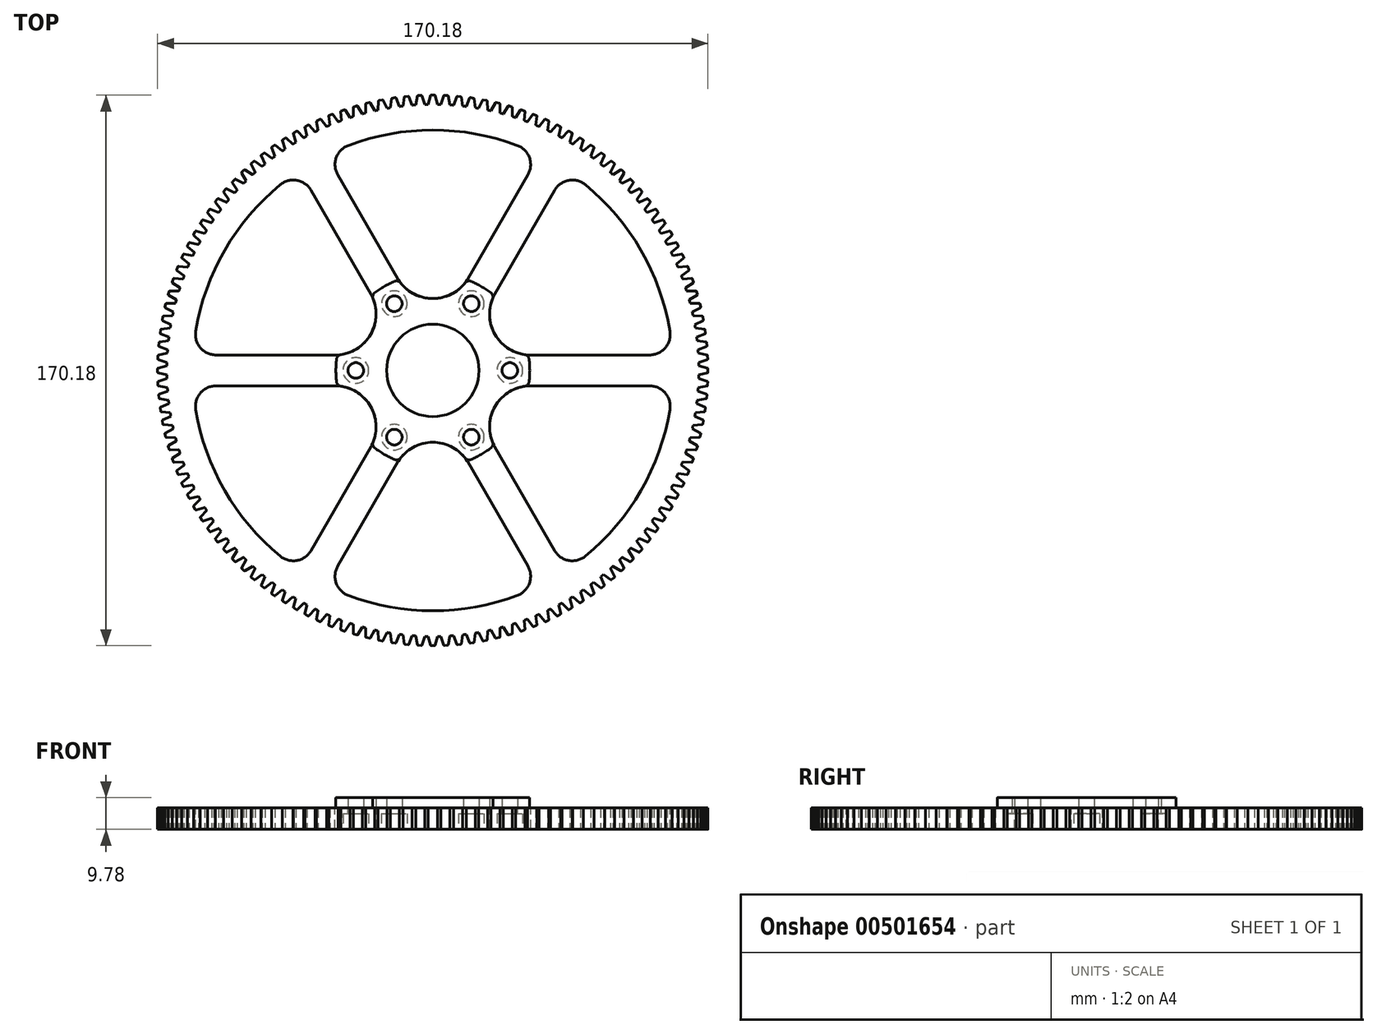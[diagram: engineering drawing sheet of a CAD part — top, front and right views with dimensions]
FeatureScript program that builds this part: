
annotation { "Feature Type Name" : "Feature", "Feature Type Description" : "" }
export const myFeature = defineFeature(function(context is Context, id is Id, definition is map)
    precondition{}
    {
        {
            var Q0;
            Q0=qCreatedBy(makeId("Top.planeOp"),FACE);
            var sketch = newSketch(context, id + "F0", { "sketchPlane" : qUnion([Q0])});
            skArc(sketch, "E0", {"start": v(-1.4, 82.23) * mm, "mid": v(-82.23, -1.4) * mm, "end": v(1.4, -82.23) * mm});
            skArc(sketch, "E1", {"start": v(1.4, -82.23) * mm, "mid": v(82.24, 0) * mm, "end": v(1.4, 82.23) * mm});
            skLineSegment(sketch, "E2", {"start": v(1.4, 82.23) * mm, "end": v(0.7, 84.97) * mm});
            skArc(sketch, "E3", {"start": v(0.7, 84.97) * mm, "mid": v(0.64, 85.06) * mm, "end": v(0.55, 85.1) * mm});
            skLineSegment(sketch, "E4", {"start": v(-1.4, 82.23) * mm, "end": v(-0.7, 84.97) * mm});
            skArc(sketch, "E5", {"start": v(-0.55, 85.1) * mm, "mid": v(-0.64, 85.06) * mm, "end": v(-0.7, 84.97) * mm});
            skLineSegment(sketch, "E6", {"start": v(-0.55, 85.1) * mm, "end": v(0.55, 85.1) * mm});
            skArc(sketch, "E7", {"start": v(1.4, 82.23) * mm, "mid": v(0, 82.24) * mm, "end": v(-1.4, 82.23) * mm});
            skSolve(sketch);
        }
        {
            var Q0;
            Q0=makeQuery(id+"F0.imprint","IMPRINT",FACE,{"disambiguationData":[TD([[makeQuery(id+"F0.imprint","IMPRINT",EDGE,{"derivedFrom":sQuery(id+"F0.wireOp",EDGE,"E0")}),1.0]])]});
            extrude(context, id + "F1", {"entities" : qUnion([Q0]), "endBound" : BoundingType.SYMMETRIC, "depth" : 6.6 * mm});
        }
        {
            var Q0;
            Q0=makeQuery(id+"F0.imprint","IMPRINT",FACE,{"disambiguationData":[TD([[makeQuery(id+"F0.imprint","IMPRINT",EDGE,{"derivedFrom":sQuery(id+"F0.wireOp",EDGE,"E2")}),1.0]])]});
            var Q1;
            Q1=makeQuery(id+"F1.opExtrude","CAP_FACE",FACE,{"disambiguationData":[OSD([sQuery(id+"F0.wireOp",EDGE,"E0"),sQuery(id+"F0.wireOp",EDGE,"E1"),sQuery(id+"F0.wireOp",EDGE,"E7")])],"isStart":false});
            var Q2;
            Q2=makeQuery(id+"F1.opExtrude","CAP_FACE",FACE,{"disambiguationData":[OSD([sQuery(id+"F0.wireOp",EDGE,"E0"),sQuery(id+"F0.wireOp",EDGE,"E1"),sQuery(id+"F0.wireOp",EDGE,"E7")])],"isStart":true});
            extrude(context, id + "F2", {"entities" : qUnion([Q0]), "endBound" : BoundingType.UP_TO_SURFACE, "endBoundEntityFace" : qUnion([Q1]), "depth" : 25.4 * mm, "hasSecondDirection" : true, "secondDirectionBound" : SecondDirectionBoundingType.UP_TO_SURFACE, "secondDirectionOppositeDirection" : true, "secondDirectionBoundEntityFace" : qUnion([Q2]), "secondDirectionDepth" : 25.4 * mm});
        }
        {
            var Q0;
            Q0=makeQuery(id+"F2.opExtrude","SWEPT_BODY",BODY,{"disambiguationData":[OSD([sQuery(id+"F0.wireOp",EDGE,"E2"),sQuery(id+"F0.wireOp",EDGE,"E3"),sQuery(id+"F0.wireOp",EDGE,"E4"),sQuery(id+"F0.wireOp",EDGE,"E5"),sQuery(id+"F0.wireOp",EDGE,"E6"),sQuery(id+"F0.wireOp",EDGE,"E7")])]});
            var Q1;
            Q1=makeQuery(id+"F1.opExtrude","CAP_EDGE",EDGE,{"disambiguationData":[OSD([sQuery(id+"F0.wireOp",EDGE,"E0"),sQuery(id+"F0.wireOp",EDGE,"E1"),sQuery(id+"F0.wireOp",EDGE,"E7")])],"isStart":false});
            circularPattern(context, id + "F3", {"operationType" : NewBodyOperationType.ADD, "entities" : qUnion([Q0]), "axis" : qUnion([Q1]), "angle" : 360 * degree, "instanceCount" : 132, "oppositeDirection" : true, "equalSpace" : true});
        }
        {
            var Q0;
            {var subQ0=sQuery(id+"F0.wireOp",EDGE,"E7");var subQ1=makeQuery(id+"F2.opExtrude","CAP_FACE",FACE,{"disambiguationData":[OSD([sQuery(id+"F0.wireOp",EDGE,"E2"),sQuery(id+"F0.wireOp",EDGE,"E3"),sQuery(id+"F0.wireOp",EDGE,"E4"),sQuery(id+"F0.wireOp",EDGE,"E5"),sQuery(id+"F0.wireOp",EDGE,"E6"),subQ0])],"isStart":false});Q0=makeQuery(id+"F3.boolean.opBoolean","MERGE",FACE,{"derivedFrom":[makeQuery(id+"F1.opExtrude","CAP_FACE",FACE,{"disambiguationData":[OSD([sQuery(id+"F0.wireOp",EDGE,"E0"),sQuery(id+"F0.wireOp",EDGE,"E1"),subQ0])],"isStart":false}),subQ1,makeQuery(id+"F3.opPattern","COPY",FACE,{"derivedFrom":subQ1,"instanceName":"1"}),makeQuery(id+"F3.opPattern","COPY",FACE,{"derivedFrom":subQ1,"instanceName":"2"}),makeQuery(id+"F3.opPattern","COPY",FACE,{"derivedFrom":subQ1,"instanceName":"3"}),makeQuery(id+"F3.opPattern","COPY",FACE,{"derivedFrom":subQ1,"instanceName":"4"}),makeQuery(id+"F3.opPattern","COPY",FACE,{"derivedFrom":subQ1,"instanceName":"5"}),makeQuery(id+"F3.opPattern","COPY",FACE,{"derivedFrom":subQ1,"instanceName":"6"}),makeQuery(id+"F3.opPattern","COPY",FACE,{"derivedFrom":subQ1,"instanceName":"7"}),makeQuery(id+"F3.opPattern","COPY",FACE,{"derivedFrom":subQ1,"instanceName":"8"}),makeQuery(id+"F3.opPattern","COPY",FACE,{"derivedFrom":subQ1,"instanceName":"9"}),makeQuery(id+"F3.opPattern","COPY",FACE,{"derivedFrom":subQ1,"instanceName":"10"}),makeQuery(id+"F3.opPattern","COPY",FACE,{"derivedFrom":subQ1,"instanceName":"11"}),makeQuery(id+"F3.opPattern","COPY",FACE,{"derivedFrom":subQ1,"instanceName":"12"}),makeQuery(id+"F3.opPattern","COPY",FACE,{"derivedFrom":subQ1,"instanceName":"13"}),makeQuery(id+"F3.opPattern","COPY",FACE,{"derivedFrom":subQ1,"instanceName":"14"}),makeQuery(id+"F3.opPattern","COPY",FACE,{"derivedFrom":subQ1,"instanceName":"15"}),makeQuery(id+"F3.opPattern","COPY",FACE,{"derivedFrom":subQ1,"instanceName":"16"}),makeQuery(id+"F3.opPattern","COPY",FACE,{"derivedFrom":subQ1,"instanceName":"17"}),makeQuery(id+"F3.opPattern","COPY",FACE,{"derivedFrom":subQ1,"instanceName":"18"}),makeQuery(id+"F3.opPattern","COPY",FACE,{"derivedFrom":subQ1,"instanceName":"19"}),makeQuery(id+"F3.opPattern","COPY",FACE,{"derivedFrom":subQ1,"instanceName":"20"}),makeQuery(id+"F3.opPattern","COPY",FACE,{"derivedFrom":subQ1,"instanceName":"21"}),makeQuery(id+"F3.opPattern","COPY",FACE,{"derivedFrom":subQ1,"instanceName":"22"}),makeQuery(id+"F3.opPattern","COPY",FACE,{"derivedFrom":subQ1,"instanceName":"23"}),makeQuery(id+"F3.opPattern","COPY",FACE,{"derivedFrom":subQ1,"instanceName":"24"}),makeQuery(id+"F3.opPattern","COPY",FACE,{"derivedFrom":subQ1,"instanceName":"25"}),makeQuery(id+"F3.opPattern","COPY",FACE,{"derivedFrom":subQ1,"instanceName":"26"}),makeQuery(id+"F3.opPattern","COPY",FACE,{"derivedFrom":subQ1,"instanceName":"27"}),makeQuery(id+"F3.opPattern","COPY",FACE,{"derivedFrom":subQ1,"instanceName":"28"}),makeQuery(id+"F3.opPattern","COPY",FACE,{"derivedFrom":subQ1,"instanceName":"29"}),makeQuery(id+"F3.opPattern","COPY",FACE,{"derivedFrom":subQ1,"instanceName":"30"}),makeQuery(id+"F3.opPattern","COPY",FACE,{"derivedFrom":subQ1,"instanceName":"31"}),makeQuery(id+"F3.opPattern","COPY",FACE,{"derivedFrom":subQ1,"instanceName":"32"}),makeQuery(id+"F3.opPattern","COPY",FACE,{"derivedFrom":subQ1,"instanceName":"33"}),makeQuery(id+"F3.opPattern","COPY",FACE,{"derivedFrom":subQ1,"instanceName":"34"}),makeQuery(id+"F3.opPattern","COPY",FACE,{"derivedFrom":subQ1,"instanceName":"35"}),makeQuery(id+"F3.opPattern","COPY",FACE,{"derivedFrom":subQ1,"instanceName":"36"}),makeQuery(id+"F3.opPattern","COPY",FACE,{"derivedFrom":subQ1,"instanceName":"37"}),makeQuery(id+"F3.opPattern","COPY",FACE,{"derivedFrom":subQ1,"instanceName":"38"}),makeQuery(id+"F3.opPattern","COPY",FACE,{"derivedFrom":subQ1,"instanceName":"39"}),makeQuery(id+"F3.opPattern","COPY",FACE,{"derivedFrom":subQ1,"instanceName":"40"}),makeQuery(id+"F3.opPattern","COPY",FACE,{"derivedFrom":subQ1,"instanceName":"41"}),makeQuery(id+"F3.opPattern","COPY",FACE,{"derivedFrom":subQ1,"instanceName":"42"}),makeQuery(id+"F3.opPattern","COPY",FACE,{"derivedFrom":subQ1,"instanceName":"43"}),makeQuery(id+"F3.opPattern","COPY",FACE,{"derivedFrom":subQ1,"instanceName":"44"}),makeQuery(id+"F3.opPattern","COPY",FACE,{"derivedFrom":subQ1,"instanceName":"45"}),makeQuery(id+"F3.opPattern","COPY",FACE,{"derivedFrom":subQ1,"instanceName":"46"}),makeQuery(id+"F3.opPattern","COPY",FACE,{"derivedFrom":subQ1,"instanceName":"47"}),makeQuery(id+"F3.opPattern","COPY",FACE,{"derivedFrom":subQ1,"instanceName":"48"}),makeQuery(id+"F3.opPattern","COPY",FACE,{"derivedFrom":subQ1,"instanceName":"49"}),makeQuery(id+"F3.opPattern","COPY",FACE,{"derivedFrom":subQ1,"instanceName":"50"}),makeQuery(id+"F3.opPattern","COPY",FACE,{"derivedFrom":subQ1,"instanceName":"51"}),makeQuery(id+"F3.opPattern","COPY",FACE,{"derivedFrom":subQ1,"instanceName":"52"}),makeQuery(id+"F3.opPattern","COPY",FACE,{"derivedFrom":subQ1,"instanceName":"53"}),makeQuery(id+"F3.opPattern","COPY",FACE,{"derivedFrom":subQ1,"instanceName":"54"}),makeQuery(id+"F3.opPattern","COPY",FACE,{"derivedFrom":subQ1,"instanceName":"55"}),makeQuery(id+"F3.opPattern","COPY",FACE,{"derivedFrom":subQ1,"instanceName":"56"}),makeQuery(id+"F3.opPattern","COPY",FACE,{"derivedFrom":subQ1,"instanceName":"57"}),makeQuery(id+"F3.opPattern","COPY",FACE,{"derivedFrom":subQ1,"instanceName":"58"}),makeQuery(id+"F3.opPattern","COPY",FACE,{"derivedFrom":subQ1,"instanceName":"59"}),makeQuery(id+"F3.opPattern","COPY",FACE,{"derivedFrom":subQ1,"instanceName":"60"}),makeQuery(id+"F3.opPattern","COPY",FACE,{"derivedFrom":subQ1,"instanceName":"61"}),makeQuery(id+"F3.opPattern","COPY",FACE,{"derivedFrom":subQ1,"instanceName":"62"}),makeQuery(id+"F3.opPattern","COPY",FACE,{"derivedFrom":subQ1,"instanceName":"63"}),makeQuery(id+"F3.opPattern","COPY",FACE,{"derivedFrom":subQ1,"instanceName":"64"}),makeQuery(id+"F3.opPattern","COPY",FACE,{"derivedFrom":subQ1,"instanceName":"65"}),makeQuery(id+"F3.opPattern","COPY",FACE,{"derivedFrom":subQ1,"instanceName":"66"}),makeQuery(id+"F3.opPattern","COPY",FACE,{"derivedFrom":subQ1,"instanceName":"67"}),makeQuery(id+"F3.opPattern","COPY",FACE,{"derivedFrom":subQ1,"instanceName":"68"}),makeQuery(id+"F3.opPattern","COPY",FACE,{"derivedFrom":subQ1,"instanceName":"69"}),makeQuery(id+"F3.opPattern","COPY",FACE,{"derivedFrom":subQ1,"instanceName":"70"}),makeQuery(id+"F3.opPattern","COPY",FACE,{"derivedFrom":subQ1,"instanceName":"71"}),makeQuery(id+"F3.opPattern","COPY",FACE,{"derivedFrom":subQ1,"instanceName":"72"}),makeQuery(id+"F3.opPattern","COPY",FACE,{"derivedFrom":subQ1,"instanceName":"73"}),makeQuery(id+"F3.opPattern","COPY",FACE,{"derivedFrom":subQ1,"instanceName":"74"}),makeQuery(id+"F3.opPattern","COPY",FACE,{"derivedFrom":subQ1,"instanceName":"75"}),makeQuery(id+"F3.opPattern","COPY",FACE,{"derivedFrom":subQ1,"instanceName":"76"}),makeQuery(id+"F3.opPattern","COPY",FACE,{"derivedFrom":subQ1,"instanceName":"77"}),makeQuery(id+"F3.opPattern","COPY",FACE,{"derivedFrom":subQ1,"instanceName":"78"}),makeQuery(id+"F3.opPattern","COPY",FACE,{"derivedFrom":subQ1,"instanceName":"79"}),makeQuery(id+"F3.opPattern","COPY",FACE,{"derivedFrom":subQ1,"instanceName":"80"}),makeQuery(id+"F3.opPattern","COPY",FACE,{"derivedFrom":subQ1,"instanceName":"81"}),makeQuery(id+"F3.opPattern","COPY",FACE,{"derivedFrom":subQ1,"instanceName":"82"}),makeQuery(id+"F3.opPattern","COPY",FACE,{"derivedFrom":subQ1,"instanceName":"83"}),makeQuery(id+"F3.opPattern","COPY",FACE,{"derivedFrom":subQ1,"instanceName":"84"}),makeQuery(id+"F3.opPattern","COPY",FACE,{"derivedFrom":subQ1,"instanceName":"85"}),makeQuery(id+"F3.opPattern","COPY",FACE,{"derivedFrom":subQ1,"instanceName":"86"}),makeQuery(id+"F3.opPattern","COPY",FACE,{"derivedFrom":subQ1,"instanceName":"87"}),makeQuery(id+"F3.opPattern","COPY",FACE,{"derivedFrom":subQ1,"instanceName":"88"}),makeQuery(id+"F3.opPattern","COPY",FACE,{"derivedFrom":subQ1,"instanceName":"89"}),makeQuery(id+"F3.opPattern","COPY",FACE,{"derivedFrom":subQ1,"instanceName":"90"}),makeQuery(id+"F3.opPattern","COPY",FACE,{"derivedFrom":subQ1,"instanceName":"91"}),makeQuery(id+"F3.opPattern","COPY",FACE,{"derivedFrom":subQ1,"instanceName":"92"}),makeQuery(id+"F3.opPattern","COPY",FACE,{"derivedFrom":subQ1,"instanceName":"93"}),makeQuery(id+"F3.opPattern","COPY",FACE,{"derivedFrom":subQ1,"instanceName":"94"}),makeQuery(id+"F3.opPattern","COPY",FACE,{"derivedFrom":subQ1,"instanceName":"95"}),makeQuery(id+"F3.opPattern","COPY",FACE,{"derivedFrom":subQ1,"instanceName":"96"}),makeQuery(id+"F3.opPattern","COPY",FACE,{"derivedFrom":subQ1,"instanceName":"97"}),makeQuery(id+"F3.opPattern","COPY",FACE,{"derivedFrom":subQ1,"instanceName":"98"}),makeQuery(id+"F3.opPattern","COPY",FACE,{"derivedFrom":subQ1,"instanceName":"99"}),makeQuery(id+"F3.opPattern","COPY",FACE,{"derivedFrom":subQ1,"instanceName":"100"}),makeQuery(id+"F3.opPattern","COPY",FACE,{"derivedFrom":subQ1,"instanceName":"101"}),makeQuery(id+"F3.opPattern","COPY",FACE,{"derivedFrom":subQ1,"instanceName":"102"}),makeQuery(id+"F3.opPattern","COPY",FACE,{"derivedFrom":subQ1,"instanceName":"103"}),makeQuery(id+"F3.opPattern","COPY",FACE,{"derivedFrom":subQ1,"instanceName":"104"}),makeQuery(id+"F3.opPattern","COPY",FACE,{"derivedFrom":subQ1,"instanceName":"105"}),makeQuery(id+"F3.opPattern","COPY",FACE,{"derivedFrom":subQ1,"instanceName":"106"}),makeQuery(id+"F3.opPattern","COPY",FACE,{"derivedFrom":subQ1,"instanceName":"107"}),makeQuery(id+"F3.opPattern","COPY",FACE,{"derivedFrom":subQ1,"instanceName":"108"}),makeQuery(id+"F3.opPattern","COPY",FACE,{"derivedFrom":subQ1,"instanceName":"109"}),makeQuery(id+"F3.opPattern","COPY",FACE,{"derivedFrom":subQ1,"instanceName":"110"}),makeQuery(id+"F3.opPattern","COPY",FACE,{"derivedFrom":subQ1,"instanceName":"111"}),makeQuery(id+"F3.opPattern","COPY",FACE,{"derivedFrom":subQ1,"instanceName":"112"}),makeQuery(id+"F3.opPattern","COPY",FACE,{"derivedFrom":subQ1,"instanceName":"113"}),makeQuery(id+"F3.opPattern","COPY",FACE,{"derivedFrom":subQ1,"instanceName":"114"}),makeQuery(id+"F3.opPattern","COPY",FACE,{"derivedFrom":subQ1,"instanceName":"115"}),makeQuery(id+"F3.opPattern","COPY",FACE,{"derivedFrom":subQ1,"instanceName":"116"}),makeQuery(id+"F3.opPattern","COPY",FACE,{"derivedFrom":subQ1,"instanceName":"117"}),makeQuery(id+"F3.opPattern","COPY",FACE,{"derivedFrom":subQ1,"instanceName":"118"}),makeQuery(id+"F3.opPattern","COPY",FACE,{"derivedFrom":subQ1,"instanceName":"119"}),makeQuery(id+"F3.opPattern","COPY",FACE,{"derivedFrom":subQ1,"instanceName":"120"}),makeQuery(id+"F3.opPattern","COPY",FACE,{"derivedFrom":subQ1,"instanceName":"121"}),makeQuery(id+"F3.opPattern","COPY",FACE,{"derivedFrom":subQ1,"instanceName":"122"}),makeQuery(id+"F3.opPattern","COPY",FACE,{"derivedFrom":subQ1,"instanceName":"123"}),makeQuery(id+"F3.opPattern","COPY",FACE,{"derivedFrom":subQ1,"instanceName":"124"}),makeQuery(id+"F3.opPattern","COPY",FACE,{"derivedFrom":subQ1,"instanceName":"125"}),makeQuery(id+"F3.opPattern","COPY",FACE,{"derivedFrom":subQ1,"instanceName":"126"}),makeQuery(id+"F3.opPattern","COPY",FACE,{"derivedFrom":subQ1,"instanceName":"127"}),makeQuery(id+"F3.opPattern","COPY",FACE,{"derivedFrom":subQ1,"instanceName":"128"}),makeQuery(id+"F3.opPattern","COPY",FACE,{"derivedFrom":subQ1,"instanceName":"129"}),makeQuery(id+"F3.opPattern","COPY",FACE,{"derivedFrom":subQ1,"instanceName":"130"}),makeQuery(id+"F3.opPattern","COPY",FACE,{"derivedFrom":subQ1,"instanceName":"131"})]});}
            var sketch = newSketch(context, id + "F4", { "sketchPlane" : qUnion([Q0])});
            skCircle(sketch, "E8", {"center": v(0, 0) * mm, "radius": 14.29 * mm});
            skCircle(sketch, "E9.cCircle", {"center": v(0, 0) * mm, "radius": 23.81 * mm, "construction": true});
            skLineSegment(sketch, "E9.0", {"start": v(23.81, 0) * mm, "end": v(11.9, -20.62) * mm, "construction": true});
            skLineSegment(sketch, "E9.1", {"start": v(11.9, -20.62) * mm, "end": v(-11.9, -20.62) * mm, "construction": true});
            skLineSegment(sketch, "E9.2", {"start": v(-11.9, -20.62) * mm, "end": v(-23.81, 0) * mm, "construction": true});
            skLineSegment(sketch, "E9.3", {"start": v(-23.81, 0) * mm, "end": v(-11.9, 20.62) * mm, "construction": true});
            skLineSegment(sketch, "E9.4", {"start": v(-11.9, 20.62) * mm, "end": v(11.9, 20.62) * mm, "construction": true});
            skLineSegment(sketch, "E9.5", {"start": v(11.9, 20.62) * mm, "end": v(23.81, 0) * mm, "construction": true});
            skCircle(sketch, "E10", {"center": v(-11.9, 20.62) * mm, "radius": 2.41 * mm});
            skCircle(sketch, "E11", {"center": v(-23.81, 0) * mm, "radius": 2.41 * mm});
            skCircle(sketch, "E12", {"center": v(-11.9, -20.62) * mm, "radius": 2.41 * mm});
            skCircle(sketch, "E13", {"center": v(11.9, -20.62) * mm, "radius": 2.41 * mm});
            skCircle(sketch, "E14", {"center": v(23.81, 0) * mm, "radius": 2.41 * mm});
            skCircle(sketch, "E15", {"center": v(11.9, 20.62) * mm, "radius": 2.41 * mm});
            skSolve(sketch);
        }
        {
            var Q0;
            Q0=qSketchRegion(id+"F4",true);
            extrude(context, id + "F5", {"entities" : qUnion([Q0]), "operationType" : NewBodyOperationType.REMOVE, "endBound" : BoundingType.THROUGH_ALL, "oppositeDirection" : true, "depth" : 25.4 * mm});
        }
        {
            var Q0;
            {var subQ0=sQuery(id+"F0.wireOp",EDGE,"E7");var subQ1=makeQuery(id+"F2.opExtrude","CAP_FACE",FACE,{"disambiguationData":[OSD([sQuery(id+"F0.wireOp",EDGE,"E2"),sQuery(id+"F0.wireOp",EDGE,"E3"),sQuery(id+"F0.wireOp",EDGE,"E4"),sQuery(id+"F0.wireOp",EDGE,"E5"),sQuery(id+"F0.wireOp",EDGE,"E6"),subQ0])],"isStart":false});Q0=makeQuery(id+"F3.boolean.opBoolean","MERGE",FACE,{"derivedFrom":[makeQuery(id+"F1.opExtrude","CAP_FACE",FACE,{"disambiguationData":[OSD([sQuery(id+"F0.wireOp",EDGE,"E0"),sQuery(id+"F0.wireOp",EDGE,"E1"),subQ0])],"isStart":false}),subQ1,makeQuery(id+"F3.opPattern","COPY",FACE,{"derivedFrom":subQ1,"instanceName":"1"}),makeQuery(id+"F3.opPattern","COPY",FACE,{"derivedFrom":subQ1,"instanceName":"2"}),makeQuery(id+"F3.opPattern","COPY",FACE,{"derivedFrom":subQ1,"instanceName":"3"}),makeQuery(id+"F3.opPattern","COPY",FACE,{"derivedFrom":subQ1,"instanceName":"4"}),makeQuery(id+"F3.opPattern","COPY",FACE,{"derivedFrom":subQ1,"instanceName":"5"}),makeQuery(id+"F3.opPattern","COPY",FACE,{"derivedFrom":subQ1,"instanceName":"6"}),makeQuery(id+"F3.opPattern","COPY",FACE,{"derivedFrom":subQ1,"instanceName":"7"}),makeQuery(id+"F3.opPattern","COPY",FACE,{"derivedFrom":subQ1,"instanceName":"8"}),makeQuery(id+"F3.opPattern","COPY",FACE,{"derivedFrom":subQ1,"instanceName":"9"}),makeQuery(id+"F3.opPattern","COPY",FACE,{"derivedFrom":subQ1,"instanceName":"10"}),makeQuery(id+"F3.opPattern","COPY",FACE,{"derivedFrom":subQ1,"instanceName":"11"}),makeQuery(id+"F3.opPattern","COPY",FACE,{"derivedFrom":subQ1,"instanceName":"12"}),makeQuery(id+"F3.opPattern","COPY",FACE,{"derivedFrom":subQ1,"instanceName":"13"}),makeQuery(id+"F3.opPattern","COPY",FACE,{"derivedFrom":subQ1,"instanceName":"14"}),makeQuery(id+"F3.opPattern","COPY",FACE,{"derivedFrom":subQ1,"instanceName":"15"}),makeQuery(id+"F3.opPattern","COPY",FACE,{"derivedFrom":subQ1,"instanceName":"16"}),makeQuery(id+"F3.opPattern","COPY",FACE,{"derivedFrom":subQ1,"instanceName":"17"}),makeQuery(id+"F3.opPattern","COPY",FACE,{"derivedFrom":subQ1,"instanceName":"18"}),makeQuery(id+"F3.opPattern","COPY",FACE,{"derivedFrom":subQ1,"instanceName":"19"}),makeQuery(id+"F3.opPattern","COPY",FACE,{"derivedFrom":subQ1,"instanceName":"20"}),makeQuery(id+"F3.opPattern","COPY",FACE,{"derivedFrom":subQ1,"instanceName":"21"}),makeQuery(id+"F3.opPattern","COPY",FACE,{"derivedFrom":subQ1,"instanceName":"22"}),makeQuery(id+"F3.opPattern","COPY",FACE,{"derivedFrom":subQ1,"instanceName":"23"}),makeQuery(id+"F3.opPattern","COPY",FACE,{"derivedFrom":subQ1,"instanceName":"24"}),makeQuery(id+"F3.opPattern","COPY",FACE,{"derivedFrom":subQ1,"instanceName":"25"}),makeQuery(id+"F3.opPattern","COPY",FACE,{"derivedFrom":subQ1,"instanceName":"26"}),makeQuery(id+"F3.opPattern","COPY",FACE,{"derivedFrom":subQ1,"instanceName":"27"}),makeQuery(id+"F3.opPattern","COPY",FACE,{"derivedFrom":subQ1,"instanceName":"28"}),makeQuery(id+"F3.opPattern","COPY",FACE,{"derivedFrom":subQ1,"instanceName":"29"}),makeQuery(id+"F3.opPattern","COPY",FACE,{"derivedFrom":subQ1,"instanceName":"30"}),makeQuery(id+"F3.opPattern","COPY",FACE,{"derivedFrom":subQ1,"instanceName":"31"}),makeQuery(id+"F3.opPattern","COPY",FACE,{"derivedFrom":subQ1,"instanceName":"32"}),makeQuery(id+"F3.opPattern","COPY",FACE,{"derivedFrom":subQ1,"instanceName":"33"}),makeQuery(id+"F3.opPattern","COPY",FACE,{"derivedFrom":subQ1,"instanceName":"34"}),makeQuery(id+"F3.opPattern","COPY",FACE,{"derivedFrom":subQ1,"instanceName":"35"}),makeQuery(id+"F3.opPattern","COPY",FACE,{"derivedFrom":subQ1,"instanceName":"36"}),makeQuery(id+"F3.opPattern","COPY",FACE,{"derivedFrom":subQ1,"instanceName":"37"}),makeQuery(id+"F3.opPattern","COPY",FACE,{"derivedFrom":subQ1,"instanceName":"38"}),makeQuery(id+"F3.opPattern","COPY",FACE,{"derivedFrom":subQ1,"instanceName":"39"}),makeQuery(id+"F3.opPattern","COPY",FACE,{"derivedFrom":subQ1,"instanceName":"40"}),makeQuery(id+"F3.opPattern","COPY",FACE,{"derivedFrom":subQ1,"instanceName":"41"}),makeQuery(id+"F3.opPattern","COPY",FACE,{"derivedFrom":subQ1,"instanceName":"42"}),makeQuery(id+"F3.opPattern","COPY",FACE,{"derivedFrom":subQ1,"instanceName":"43"}),makeQuery(id+"F3.opPattern","COPY",FACE,{"derivedFrom":subQ1,"instanceName":"44"}),makeQuery(id+"F3.opPattern","COPY",FACE,{"derivedFrom":subQ1,"instanceName":"45"}),makeQuery(id+"F3.opPattern","COPY",FACE,{"derivedFrom":subQ1,"instanceName":"46"}),makeQuery(id+"F3.opPattern","COPY",FACE,{"derivedFrom":subQ1,"instanceName":"47"}),makeQuery(id+"F3.opPattern","COPY",FACE,{"derivedFrom":subQ1,"instanceName":"48"}),makeQuery(id+"F3.opPattern","COPY",FACE,{"derivedFrom":subQ1,"instanceName":"49"}),makeQuery(id+"F3.opPattern","COPY",FACE,{"derivedFrom":subQ1,"instanceName":"50"}),makeQuery(id+"F3.opPattern","COPY",FACE,{"derivedFrom":subQ1,"instanceName":"51"}),makeQuery(id+"F3.opPattern","COPY",FACE,{"derivedFrom":subQ1,"instanceName":"52"}),makeQuery(id+"F3.opPattern","COPY",FACE,{"derivedFrom":subQ1,"instanceName":"53"}),makeQuery(id+"F3.opPattern","COPY",FACE,{"derivedFrom":subQ1,"instanceName":"54"}),makeQuery(id+"F3.opPattern","COPY",FACE,{"derivedFrom":subQ1,"instanceName":"55"}),makeQuery(id+"F3.opPattern","COPY",FACE,{"derivedFrom":subQ1,"instanceName":"56"}),makeQuery(id+"F3.opPattern","COPY",FACE,{"derivedFrom":subQ1,"instanceName":"57"}),makeQuery(id+"F3.opPattern","COPY",FACE,{"derivedFrom":subQ1,"instanceName":"58"}),makeQuery(id+"F3.opPattern","COPY",FACE,{"derivedFrom":subQ1,"instanceName":"59"}),makeQuery(id+"F3.opPattern","COPY",FACE,{"derivedFrom":subQ1,"instanceName":"60"}),makeQuery(id+"F3.opPattern","COPY",FACE,{"derivedFrom":subQ1,"instanceName":"61"}),makeQuery(id+"F3.opPattern","COPY",FACE,{"derivedFrom":subQ1,"instanceName":"62"}),makeQuery(id+"F3.opPattern","COPY",FACE,{"derivedFrom":subQ1,"instanceName":"63"}),makeQuery(id+"F3.opPattern","COPY",FACE,{"derivedFrom":subQ1,"instanceName":"64"}),makeQuery(id+"F3.opPattern","COPY",FACE,{"derivedFrom":subQ1,"instanceName":"65"}),makeQuery(id+"F3.opPattern","COPY",FACE,{"derivedFrom":subQ1,"instanceName":"66"}),makeQuery(id+"F3.opPattern","COPY",FACE,{"derivedFrom":subQ1,"instanceName":"67"}),makeQuery(id+"F3.opPattern","COPY",FACE,{"derivedFrom":subQ1,"instanceName":"68"}),makeQuery(id+"F3.opPattern","COPY",FACE,{"derivedFrom":subQ1,"instanceName":"69"}),makeQuery(id+"F3.opPattern","COPY",FACE,{"derivedFrom":subQ1,"instanceName":"70"}),makeQuery(id+"F3.opPattern","COPY",FACE,{"derivedFrom":subQ1,"instanceName":"71"}),makeQuery(id+"F3.opPattern","COPY",FACE,{"derivedFrom":subQ1,"instanceName":"72"}),makeQuery(id+"F3.opPattern","COPY",FACE,{"derivedFrom":subQ1,"instanceName":"73"}),makeQuery(id+"F3.opPattern","COPY",FACE,{"derivedFrom":subQ1,"instanceName":"74"}),makeQuery(id+"F3.opPattern","COPY",FACE,{"derivedFrom":subQ1,"instanceName":"75"}),makeQuery(id+"F3.opPattern","COPY",FACE,{"derivedFrom":subQ1,"instanceName":"76"}),makeQuery(id+"F3.opPattern","COPY",FACE,{"derivedFrom":subQ1,"instanceName":"77"}),makeQuery(id+"F3.opPattern","COPY",FACE,{"derivedFrom":subQ1,"instanceName":"78"}),makeQuery(id+"F3.opPattern","COPY",FACE,{"derivedFrom":subQ1,"instanceName":"79"}),makeQuery(id+"F3.opPattern","COPY",FACE,{"derivedFrom":subQ1,"instanceName":"80"}),makeQuery(id+"F3.opPattern","COPY",FACE,{"derivedFrom":subQ1,"instanceName":"81"}),makeQuery(id+"F3.opPattern","COPY",FACE,{"derivedFrom":subQ1,"instanceName":"82"}),makeQuery(id+"F3.opPattern","COPY",FACE,{"derivedFrom":subQ1,"instanceName":"83"}),makeQuery(id+"F3.opPattern","COPY",FACE,{"derivedFrom":subQ1,"instanceName":"84"}),makeQuery(id+"F3.opPattern","COPY",FACE,{"derivedFrom":subQ1,"instanceName":"85"}),makeQuery(id+"F3.opPattern","COPY",FACE,{"derivedFrom":subQ1,"instanceName":"86"}),makeQuery(id+"F3.opPattern","COPY",FACE,{"derivedFrom":subQ1,"instanceName":"87"}),makeQuery(id+"F3.opPattern","COPY",FACE,{"derivedFrom":subQ1,"instanceName":"88"}),makeQuery(id+"F3.opPattern","COPY",FACE,{"derivedFrom":subQ1,"instanceName":"89"}),makeQuery(id+"F3.opPattern","COPY",FACE,{"derivedFrom":subQ1,"instanceName":"90"}),makeQuery(id+"F3.opPattern","COPY",FACE,{"derivedFrom":subQ1,"instanceName":"91"}),makeQuery(id+"F3.opPattern","COPY",FACE,{"derivedFrom":subQ1,"instanceName":"92"}),makeQuery(id+"F3.opPattern","COPY",FACE,{"derivedFrom":subQ1,"instanceName":"93"}),makeQuery(id+"F3.opPattern","COPY",FACE,{"derivedFrom":subQ1,"instanceName":"94"}),makeQuery(id+"F3.opPattern","COPY",FACE,{"derivedFrom":subQ1,"instanceName":"95"}),makeQuery(id+"F3.opPattern","COPY",FACE,{"derivedFrom":subQ1,"instanceName":"96"}),makeQuery(id+"F3.opPattern","COPY",FACE,{"derivedFrom":subQ1,"instanceName":"97"}),makeQuery(id+"F3.opPattern","COPY",FACE,{"derivedFrom":subQ1,"instanceName":"98"}),makeQuery(id+"F3.opPattern","COPY",FACE,{"derivedFrom":subQ1,"instanceName":"99"}),makeQuery(id+"F3.opPattern","COPY",FACE,{"derivedFrom":subQ1,"instanceName":"100"}),makeQuery(id+"F3.opPattern","COPY",FACE,{"derivedFrom":subQ1,"instanceName":"101"}),makeQuery(id+"F3.opPattern","COPY",FACE,{"derivedFrom":subQ1,"instanceName":"102"}),makeQuery(id+"F3.opPattern","COPY",FACE,{"derivedFrom":subQ1,"instanceName":"103"}),makeQuery(id+"F3.opPattern","COPY",FACE,{"derivedFrom":subQ1,"instanceName":"104"}),makeQuery(id+"F3.opPattern","COPY",FACE,{"derivedFrom":subQ1,"instanceName":"105"}),makeQuery(id+"F3.opPattern","COPY",FACE,{"derivedFrom":subQ1,"instanceName":"106"}),makeQuery(id+"F3.opPattern","COPY",FACE,{"derivedFrom":subQ1,"instanceName":"107"}),makeQuery(id+"F3.opPattern","COPY",FACE,{"derivedFrom":subQ1,"instanceName":"108"}),makeQuery(id+"F3.opPattern","COPY",FACE,{"derivedFrom":subQ1,"instanceName":"109"}),makeQuery(id+"F3.opPattern","COPY",FACE,{"derivedFrom":subQ1,"instanceName":"110"}),makeQuery(id+"F3.opPattern","COPY",FACE,{"derivedFrom":subQ1,"instanceName":"111"}),makeQuery(id+"F3.opPattern","COPY",FACE,{"derivedFrom":subQ1,"instanceName":"112"}),makeQuery(id+"F3.opPattern","COPY",FACE,{"derivedFrom":subQ1,"instanceName":"113"}),makeQuery(id+"F3.opPattern","COPY",FACE,{"derivedFrom":subQ1,"instanceName":"114"}),makeQuery(id+"F3.opPattern","COPY",FACE,{"derivedFrom":subQ1,"instanceName":"115"}),makeQuery(id+"F3.opPattern","COPY",FACE,{"derivedFrom":subQ1,"instanceName":"116"}),makeQuery(id+"F3.opPattern","COPY",FACE,{"derivedFrom":subQ1,"instanceName":"117"}),makeQuery(id+"F3.opPattern","COPY",FACE,{"derivedFrom":subQ1,"instanceName":"118"}),makeQuery(id+"F3.opPattern","COPY",FACE,{"derivedFrom":subQ1,"instanceName":"119"}),makeQuery(id+"F3.opPattern","COPY",FACE,{"derivedFrom":subQ1,"instanceName":"120"}),makeQuery(id+"F3.opPattern","COPY",FACE,{"derivedFrom":subQ1,"instanceName":"121"}),makeQuery(id+"F3.opPattern","COPY",FACE,{"derivedFrom":subQ1,"instanceName":"122"}),makeQuery(id+"F3.opPattern","COPY",FACE,{"derivedFrom":subQ1,"instanceName":"123"}),makeQuery(id+"F3.opPattern","COPY",FACE,{"derivedFrom":subQ1,"instanceName":"124"}),makeQuery(id+"F3.opPattern","COPY",FACE,{"derivedFrom":subQ1,"instanceName":"125"}),makeQuery(id+"F3.opPattern","COPY",FACE,{"derivedFrom":subQ1,"instanceName":"126"}),makeQuery(id+"F3.opPattern","COPY",FACE,{"derivedFrom":subQ1,"instanceName":"127"}),makeQuery(id+"F3.opPattern","COPY",FACE,{"derivedFrom":subQ1,"instanceName":"128"}),makeQuery(id+"F3.opPattern","COPY",FACE,{"derivedFrom":subQ1,"instanceName":"129"}),makeQuery(id+"F3.opPattern","COPY",FACE,{"derivedFrom":subQ1,"instanceName":"130"}),makeQuery(id+"F3.opPattern","COPY",FACE,{"derivedFrom":subQ1,"instanceName":"131"})]});}
            var sketch = newSketch(context, id + "F6", { "sketchPlane" : qUnion([Q0])});
            skArc(sketch, "E16", {"start": v(-37.15, 64.35) * mm, "mid": v(-64.35, 37.15) * mm, "end": v(-74.3, 0) * mm});
            skArc(sketch, "E17", {"start": v(-15.08, 26.12) * mm, "mid": v(-26.12, 15.08) * mm, "end": v(-30.16, 0) * mm});
            skLineSegment(sketch, "E18", {"start": v(-15.08, 26.12) * mm, "end": v(-37.15, 64.35) * mm, "construction": true});
            skLineSegment(sketch, "E19", {"start": v(-30.16, 0) * mm, "end": v(-74.3, 0) * mm, "construction": true});
            skPoint(sketch, "E20", {"position": v(-23.81, 0) * mm});
            skLineSegment(sketch, "E21.0", {"start": v(-29.78, 4.77) * mm, "end": v(-74.15, 4.77) * mm});
            skLineSegment(sketch, "E22.0", {"start": v(-19.02, 23.4) * mm, "end": v(-41.2, 61.83) * mm});
            skPoint(sketch, "E23", {"position": v(-11.9, 20.62) * mm});
            skArc(sketch, "E24", {"start": v(-29.78, 4.77) * mm, "mid": v(-19.25, 11.11) * mm, "end": v(-19.02, 23.4) * mm});
            skCircle(sketch, "E25", {"center": v(0, 0) * mm, "radius": 34.93 * mm, "construction": true});
            skLineSegment(sketch, "E26", {"start": v(-26.12, 15.08) * mm, "end": v(0, 0) * mm, "construction": true});
            skSolve(sketch);
        }
        {
            var Q0;
            {var subQ0=sQuery(id+"F6.wireOp",EDGE,"E21.0");Q0=makeQuery(id+"F6.imprint","IMPRINT",FACE,{"disambiguationData":[TD([[makeQuery(id+"F6.imprint","IMPRINT",EDGE,{"derivedFrom":subQ0}),-1.0]])]});}
            var Q1;
            {var subQ0=sQuery(id+"F6.wireOp",EDGE,"E24");Q1=makeQuery(id+"F6.imprint","IMPRINT",FACE,{"disambiguationData":[TD([[makeQuery(id+"F6.imprint","IMPRINT",EDGE,{"derivedFrom":subQ0}),1.0]])]});}
            var Q2;
            {var subQ0=sQuery(id+"F0.wireOp",EDGE,"E7");var subQ1=makeQuery(id+"F2.opExtrude","CAP_FACE",FACE,{"disambiguationData":[OSD([sQuery(id+"F0.wireOp",EDGE,"E2"),sQuery(id+"F0.wireOp",EDGE,"E3"),sQuery(id+"F0.wireOp",EDGE,"E4"),sQuery(id+"F0.wireOp",EDGE,"E5"),sQuery(id+"F0.wireOp",EDGE,"E6"),subQ0])],"isStart":true});Q2=makeQuery(id+"F3.boolean.opBoolean","MERGE",FACE,{"derivedFrom":[makeQuery(id+"F1.opExtrude","CAP_FACE",FACE,{"disambiguationData":[OSD([sQuery(id+"F0.wireOp",EDGE,"E0"),sQuery(id+"F0.wireOp",EDGE,"E1"),subQ0])],"isStart":true}),subQ1,makeQuery(id+"F3.opPattern","COPY",FACE,{"derivedFrom":subQ1,"instanceName":"1"}),makeQuery(id+"F3.opPattern","COPY",FACE,{"derivedFrom":subQ1,"instanceName":"2"}),makeQuery(id+"F3.opPattern","COPY",FACE,{"derivedFrom":subQ1,"instanceName":"3"}),makeQuery(id+"F3.opPattern","COPY",FACE,{"derivedFrom":subQ1,"instanceName":"4"}),makeQuery(id+"F3.opPattern","COPY",FACE,{"derivedFrom":subQ1,"instanceName":"5"}),makeQuery(id+"F3.opPattern","COPY",FACE,{"derivedFrom":subQ1,"instanceName":"6"}),makeQuery(id+"F3.opPattern","COPY",FACE,{"derivedFrom":subQ1,"instanceName":"7"}),makeQuery(id+"F3.opPattern","COPY",FACE,{"derivedFrom":subQ1,"instanceName":"8"}),makeQuery(id+"F3.opPattern","COPY",FACE,{"derivedFrom":subQ1,"instanceName":"9"}),makeQuery(id+"F3.opPattern","COPY",FACE,{"derivedFrom":subQ1,"instanceName":"10"}),makeQuery(id+"F3.opPattern","COPY",FACE,{"derivedFrom":subQ1,"instanceName":"11"}),makeQuery(id+"F3.opPattern","COPY",FACE,{"derivedFrom":subQ1,"instanceName":"12"}),makeQuery(id+"F3.opPattern","COPY",FACE,{"derivedFrom":subQ1,"instanceName":"13"}),makeQuery(id+"F3.opPattern","COPY",FACE,{"derivedFrom":subQ1,"instanceName":"14"}),makeQuery(id+"F3.opPattern","COPY",FACE,{"derivedFrom":subQ1,"instanceName":"15"}),makeQuery(id+"F3.opPattern","COPY",FACE,{"derivedFrom":subQ1,"instanceName":"16"}),makeQuery(id+"F3.opPattern","COPY",FACE,{"derivedFrom":subQ1,"instanceName":"17"}),makeQuery(id+"F3.opPattern","COPY",FACE,{"derivedFrom":subQ1,"instanceName":"18"}),makeQuery(id+"F3.opPattern","COPY",FACE,{"derivedFrom":subQ1,"instanceName":"19"}),makeQuery(id+"F3.opPattern","COPY",FACE,{"derivedFrom":subQ1,"instanceName":"20"}),makeQuery(id+"F3.opPattern","COPY",FACE,{"derivedFrom":subQ1,"instanceName":"21"}),makeQuery(id+"F3.opPattern","COPY",FACE,{"derivedFrom":subQ1,"instanceName":"22"}),makeQuery(id+"F3.opPattern","COPY",FACE,{"derivedFrom":subQ1,"instanceName":"23"}),makeQuery(id+"F3.opPattern","COPY",FACE,{"derivedFrom":subQ1,"instanceName":"24"}),makeQuery(id+"F3.opPattern","COPY",FACE,{"derivedFrom":subQ1,"instanceName":"25"}),makeQuery(id+"F3.opPattern","COPY",FACE,{"derivedFrom":subQ1,"instanceName":"26"}),makeQuery(id+"F3.opPattern","COPY",FACE,{"derivedFrom":subQ1,"instanceName":"27"}),makeQuery(id+"F3.opPattern","COPY",FACE,{"derivedFrom":subQ1,"instanceName":"28"}),makeQuery(id+"F3.opPattern","COPY",FACE,{"derivedFrom":subQ1,"instanceName":"29"}),makeQuery(id+"F3.opPattern","COPY",FACE,{"derivedFrom":subQ1,"instanceName":"30"}),makeQuery(id+"F3.opPattern","COPY",FACE,{"derivedFrom":subQ1,"instanceName":"31"}),makeQuery(id+"F3.opPattern","COPY",FACE,{"derivedFrom":subQ1,"instanceName":"32"}),makeQuery(id+"F3.opPattern","COPY",FACE,{"derivedFrom":subQ1,"instanceName":"33"}),makeQuery(id+"F3.opPattern","COPY",FACE,{"derivedFrom":subQ1,"instanceName":"34"}),makeQuery(id+"F3.opPattern","COPY",FACE,{"derivedFrom":subQ1,"instanceName":"35"}),makeQuery(id+"F3.opPattern","COPY",FACE,{"derivedFrom":subQ1,"instanceName":"36"}),makeQuery(id+"F3.opPattern","COPY",FACE,{"derivedFrom":subQ1,"instanceName":"37"}),makeQuery(id+"F3.opPattern","COPY",FACE,{"derivedFrom":subQ1,"instanceName":"38"}),makeQuery(id+"F3.opPattern","COPY",FACE,{"derivedFrom":subQ1,"instanceName":"39"}),makeQuery(id+"F3.opPattern","COPY",FACE,{"derivedFrom":subQ1,"instanceName":"40"}),makeQuery(id+"F3.opPattern","COPY",FACE,{"derivedFrom":subQ1,"instanceName":"41"}),makeQuery(id+"F3.opPattern","COPY",FACE,{"derivedFrom":subQ1,"instanceName":"42"}),makeQuery(id+"F3.opPattern","COPY",FACE,{"derivedFrom":subQ1,"instanceName":"43"}),makeQuery(id+"F3.opPattern","COPY",FACE,{"derivedFrom":subQ1,"instanceName":"44"}),makeQuery(id+"F3.opPattern","COPY",FACE,{"derivedFrom":subQ1,"instanceName":"45"}),makeQuery(id+"F3.opPattern","COPY",FACE,{"derivedFrom":subQ1,"instanceName":"46"}),makeQuery(id+"F3.opPattern","COPY",FACE,{"derivedFrom":subQ1,"instanceName":"47"}),makeQuery(id+"F3.opPattern","COPY",FACE,{"derivedFrom":subQ1,"instanceName":"48"}),makeQuery(id+"F3.opPattern","COPY",FACE,{"derivedFrom":subQ1,"instanceName":"49"}),makeQuery(id+"F3.opPattern","COPY",FACE,{"derivedFrom":subQ1,"instanceName":"50"}),makeQuery(id+"F3.opPattern","COPY",FACE,{"derivedFrom":subQ1,"instanceName":"51"}),makeQuery(id+"F3.opPattern","COPY",FACE,{"derivedFrom":subQ1,"instanceName":"52"}),makeQuery(id+"F3.opPattern","COPY",FACE,{"derivedFrom":subQ1,"instanceName":"53"}),makeQuery(id+"F3.opPattern","COPY",FACE,{"derivedFrom":subQ1,"instanceName":"54"}),makeQuery(id+"F3.opPattern","COPY",FACE,{"derivedFrom":subQ1,"instanceName":"55"}),makeQuery(id+"F3.opPattern","COPY",FACE,{"derivedFrom":subQ1,"instanceName":"56"}),makeQuery(id+"F3.opPattern","COPY",FACE,{"derivedFrom":subQ1,"instanceName":"57"}),makeQuery(id+"F3.opPattern","COPY",FACE,{"derivedFrom":subQ1,"instanceName":"58"}),makeQuery(id+"F3.opPattern","COPY",FACE,{"derivedFrom":subQ1,"instanceName":"59"}),makeQuery(id+"F3.opPattern","COPY",FACE,{"derivedFrom":subQ1,"instanceName":"60"}),makeQuery(id+"F3.opPattern","COPY",FACE,{"derivedFrom":subQ1,"instanceName":"61"}),makeQuery(id+"F3.opPattern","COPY",FACE,{"derivedFrom":subQ1,"instanceName":"62"}),makeQuery(id+"F3.opPattern","COPY",FACE,{"derivedFrom":subQ1,"instanceName":"63"}),makeQuery(id+"F3.opPattern","COPY",FACE,{"derivedFrom":subQ1,"instanceName":"64"}),makeQuery(id+"F3.opPattern","COPY",FACE,{"derivedFrom":subQ1,"instanceName":"65"}),makeQuery(id+"F3.opPattern","COPY",FACE,{"derivedFrom":subQ1,"instanceName":"66"}),makeQuery(id+"F3.opPattern","COPY",FACE,{"derivedFrom":subQ1,"instanceName":"67"}),makeQuery(id+"F3.opPattern","COPY",FACE,{"derivedFrom":subQ1,"instanceName":"68"}),makeQuery(id+"F3.opPattern","COPY",FACE,{"derivedFrom":subQ1,"instanceName":"69"}),makeQuery(id+"F3.opPattern","COPY",FACE,{"derivedFrom":subQ1,"instanceName":"70"}),makeQuery(id+"F3.opPattern","COPY",FACE,{"derivedFrom":subQ1,"instanceName":"71"}),makeQuery(id+"F3.opPattern","COPY",FACE,{"derivedFrom":subQ1,"instanceName":"72"}),makeQuery(id+"F3.opPattern","COPY",FACE,{"derivedFrom":subQ1,"instanceName":"73"}),makeQuery(id+"F3.opPattern","COPY",FACE,{"derivedFrom":subQ1,"instanceName":"74"}),makeQuery(id+"F3.opPattern","COPY",FACE,{"derivedFrom":subQ1,"instanceName":"75"}),makeQuery(id+"F3.opPattern","COPY",FACE,{"derivedFrom":subQ1,"instanceName":"76"}),makeQuery(id+"F3.opPattern","COPY",FACE,{"derivedFrom":subQ1,"instanceName":"77"}),makeQuery(id+"F3.opPattern","COPY",FACE,{"derivedFrom":subQ1,"instanceName":"78"}),makeQuery(id+"F3.opPattern","COPY",FACE,{"derivedFrom":subQ1,"instanceName":"79"}),makeQuery(id+"F3.opPattern","COPY",FACE,{"derivedFrom":subQ1,"instanceName":"80"}),makeQuery(id+"F3.opPattern","COPY",FACE,{"derivedFrom":subQ1,"instanceName":"81"}),makeQuery(id+"F3.opPattern","COPY",FACE,{"derivedFrom":subQ1,"instanceName":"82"}),makeQuery(id+"F3.opPattern","COPY",FACE,{"derivedFrom":subQ1,"instanceName":"83"}),makeQuery(id+"F3.opPattern","COPY",FACE,{"derivedFrom":subQ1,"instanceName":"84"}),makeQuery(id+"F3.opPattern","COPY",FACE,{"derivedFrom":subQ1,"instanceName":"85"}),makeQuery(id+"F3.opPattern","COPY",FACE,{"derivedFrom":subQ1,"instanceName":"86"}),makeQuery(id+"F3.opPattern","COPY",FACE,{"derivedFrom":subQ1,"instanceName":"87"}),makeQuery(id+"F3.opPattern","COPY",FACE,{"derivedFrom":subQ1,"instanceName":"88"}),makeQuery(id+"F3.opPattern","COPY",FACE,{"derivedFrom":subQ1,"instanceName":"89"}),makeQuery(id+"F3.opPattern","COPY",FACE,{"derivedFrom":subQ1,"instanceName":"90"}),makeQuery(id+"F3.opPattern","COPY",FACE,{"derivedFrom":subQ1,"instanceName":"91"}),makeQuery(id+"F3.opPattern","COPY",FACE,{"derivedFrom":subQ1,"instanceName":"92"}),makeQuery(id+"F3.opPattern","COPY",FACE,{"derivedFrom":subQ1,"instanceName":"93"}),makeQuery(id+"F3.opPattern","COPY",FACE,{"derivedFrom":subQ1,"instanceName":"94"}),makeQuery(id+"F3.opPattern","COPY",FACE,{"derivedFrom":subQ1,"instanceName":"95"}),makeQuery(id+"F3.opPattern","COPY",FACE,{"derivedFrom":subQ1,"instanceName":"96"}),makeQuery(id+"F3.opPattern","COPY",FACE,{"derivedFrom":subQ1,"instanceName":"97"}),makeQuery(id+"F3.opPattern","COPY",FACE,{"derivedFrom":subQ1,"instanceName":"98"}),makeQuery(id+"F3.opPattern","COPY",FACE,{"derivedFrom":subQ1,"instanceName":"99"}),makeQuery(id+"F3.opPattern","COPY",FACE,{"derivedFrom":subQ1,"instanceName":"100"}),makeQuery(id+"F3.opPattern","COPY",FACE,{"derivedFrom":subQ1,"instanceName":"101"}),makeQuery(id+"F3.opPattern","COPY",FACE,{"derivedFrom":subQ1,"instanceName":"102"}),makeQuery(id+"F3.opPattern","COPY",FACE,{"derivedFrom":subQ1,"instanceName":"103"}),makeQuery(id+"F3.opPattern","COPY",FACE,{"derivedFrom":subQ1,"instanceName":"104"}),makeQuery(id+"F3.opPattern","COPY",FACE,{"derivedFrom":subQ1,"instanceName":"105"}),makeQuery(id+"F3.opPattern","COPY",FACE,{"derivedFrom":subQ1,"instanceName":"106"}),makeQuery(id+"F3.opPattern","COPY",FACE,{"derivedFrom":subQ1,"instanceName":"107"}),makeQuery(id+"F3.opPattern","COPY",FACE,{"derivedFrom":subQ1,"instanceName":"108"}),makeQuery(id+"F3.opPattern","COPY",FACE,{"derivedFrom":subQ1,"instanceName":"109"}),makeQuery(id+"F3.opPattern","COPY",FACE,{"derivedFrom":subQ1,"instanceName":"110"}),makeQuery(id+"F3.opPattern","COPY",FACE,{"derivedFrom":subQ1,"instanceName":"111"}),makeQuery(id+"F3.opPattern","COPY",FACE,{"derivedFrom":subQ1,"instanceName":"112"}),makeQuery(id+"F3.opPattern","COPY",FACE,{"derivedFrom":subQ1,"instanceName":"113"}),makeQuery(id+"F3.opPattern","COPY",FACE,{"derivedFrom":subQ1,"instanceName":"114"}),makeQuery(id+"F3.opPattern","COPY",FACE,{"derivedFrom":subQ1,"instanceName":"115"}),makeQuery(id+"F3.opPattern","COPY",FACE,{"derivedFrom":subQ1,"instanceName":"116"}),makeQuery(id+"F3.opPattern","COPY",FACE,{"derivedFrom":subQ1,"instanceName":"117"}),makeQuery(id+"F3.opPattern","COPY",FACE,{"derivedFrom":subQ1,"instanceName":"118"}),makeQuery(id+"F3.opPattern","COPY",FACE,{"derivedFrom":subQ1,"instanceName":"119"}),makeQuery(id+"F3.opPattern","COPY",FACE,{"derivedFrom":subQ1,"instanceName":"120"}),makeQuery(id+"F3.opPattern","COPY",FACE,{"derivedFrom":subQ1,"instanceName":"121"}),makeQuery(id+"F3.opPattern","COPY",FACE,{"derivedFrom":subQ1,"instanceName":"122"}),makeQuery(id+"F3.opPattern","COPY",FACE,{"derivedFrom":subQ1,"instanceName":"123"}),makeQuery(id+"F3.opPattern","COPY",FACE,{"derivedFrom":subQ1,"instanceName":"124"}),makeQuery(id+"F3.opPattern","COPY",FACE,{"derivedFrom":subQ1,"instanceName":"125"}),makeQuery(id+"F3.opPattern","COPY",FACE,{"derivedFrom":subQ1,"instanceName":"126"}),makeQuery(id+"F3.opPattern","COPY",FACE,{"derivedFrom":subQ1,"instanceName":"127"}),makeQuery(id+"F3.opPattern","COPY",FACE,{"derivedFrom":subQ1,"instanceName":"128"}),makeQuery(id+"F3.opPattern","COPY",FACE,{"derivedFrom":subQ1,"instanceName":"129"}),makeQuery(id+"F3.opPattern","COPY",FACE,{"derivedFrom":subQ1,"instanceName":"130"}),makeQuery(id+"F3.opPattern","COPY",FACE,{"derivedFrom":subQ1,"instanceName":"131"})]});}
            extrude(context, id + "F7", {"entities" : qUnion([Q0, Q1]), "endBound" : BoundingType.UP_TO_SURFACE, "oppositeDirection" : true, "endBoundEntityFace" : qUnion([Q2]), "depth" : 25.4 * mm});
        }
        {
            var Q0;
            Q0=makeQuery(id+"F7.opExtrude","SWEPT_EDGE",EDGE,{"disambiguationData":[OSD([sQuery(id+"F6.wireOp",EDGE,"E16"),sQuery(id+"F6.wireOp",EDGE,"E21.0")])]});
            var Q1;
            Q1=makeQuery(id+"F7.opExtrude","SWEPT_EDGE",EDGE,{"disambiguationData":[OSD([sQuery(id+"F6.wireOp",EDGE,"E17"),sQuery(id+"F6.wireOp",EDGE,"E21.0")])]});
            var Q2;
            Q2=makeQuery(id+"F7.opExtrude","SWEPT_EDGE",EDGE,{"disambiguationData":[OSD([sQuery(id+"F6.wireOp",EDGE,"E17"),sQuery(id+"F6.wireOp",EDGE,"E22.0")])]});
            var Q3;
            Q3=makeQuery(id+"F7.opExtrude","SWEPT_EDGE",EDGE,{"disambiguationData":[OSD([sQuery(id+"F6.wireOp",EDGE,"E16"),sQuery(id+"F6.wireOp",EDGE,"E22.0")])]});
            fillet(context, id + "F8", {"entities" : qUnion([Q0, Q1, Q2, Q3]), "radius" : 6.35 * mm, "tangentPropagation" : true, "allowEdgeOverflow" : false});
        }
        {
            var Q0;
            Q0=makeQuery(id+"F7.opExtrude","SWEPT_BODY",BODY,{"disambiguationData":[OSD([sQuery(id+"F6.wireOp",EDGE,"E16"),sQuery(id+"F6.wireOp",EDGE,"E17"),sQuery(id+"F6.wireOp",EDGE,"E21.0"),sQuery(id+"F6.wireOp",EDGE,"E22.0")])]});
            var Q1;
            Q1=makeQuery(id+"F5.boolean.opBoolean","COPY",FACE,{"derivedFrom":makeQuery(id+"F5.opExtrude","SWEPT_FACE",FACE,{"disambiguationData":[OSD([sQuery(id+"F4.wireOp",EDGE,"E8")])]})});
            circularPattern(context, id + "F9", {"operationType" : NewBodyOperationType.REMOVE, "entities" : qUnion([Q0]), "axis" : qUnion([Q1]), "angle" : 360 * degree, "instanceCount" : 6, "equalSpace" : true});
        }
        {
            var Q0;
            {var subQ0=sQuery(id+"F0.wireOp",EDGE,"E7");var subQ1=makeQuery(id+"F2.opExtrude","CAP_FACE",FACE,{"disambiguationData":[OSD([sQuery(id+"F0.wireOp",EDGE,"E2"),sQuery(id+"F0.wireOp",EDGE,"E3"),sQuery(id+"F0.wireOp",EDGE,"E4"),sQuery(id+"F0.wireOp",EDGE,"E5"),sQuery(id+"F0.wireOp",EDGE,"E6"),subQ0])],"isStart":false});Q0=makeQuery(id+"F3.boolean.opBoolean","MERGE",FACE,{"derivedFrom":[makeQuery(id+"F1.opExtrude","CAP_FACE",FACE,{"disambiguationData":[OSD([sQuery(id+"F0.wireOp",EDGE,"E0"),sQuery(id+"F0.wireOp",EDGE,"E1"),subQ0])],"isStart":false}),subQ1,makeQuery(id+"F3.opPattern","COPY",FACE,{"derivedFrom":subQ1,"instanceName":"1"}),makeQuery(id+"F3.opPattern","COPY",FACE,{"derivedFrom":subQ1,"instanceName":"2"}),makeQuery(id+"F3.opPattern","COPY",FACE,{"derivedFrom":subQ1,"instanceName":"3"}),makeQuery(id+"F3.opPattern","COPY",FACE,{"derivedFrom":subQ1,"instanceName":"4"}),makeQuery(id+"F3.opPattern","COPY",FACE,{"derivedFrom":subQ1,"instanceName":"5"}),makeQuery(id+"F3.opPattern","COPY",FACE,{"derivedFrom":subQ1,"instanceName":"6"}),makeQuery(id+"F3.opPattern","COPY",FACE,{"derivedFrom":subQ1,"instanceName":"7"}),makeQuery(id+"F3.opPattern","COPY",FACE,{"derivedFrom":subQ1,"instanceName":"8"}),makeQuery(id+"F3.opPattern","COPY",FACE,{"derivedFrom":subQ1,"instanceName":"9"}),makeQuery(id+"F3.opPattern","COPY",FACE,{"derivedFrom":subQ1,"instanceName":"10"}),makeQuery(id+"F3.opPattern","COPY",FACE,{"derivedFrom":subQ1,"instanceName":"11"}),makeQuery(id+"F3.opPattern","COPY",FACE,{"derivedFrom":subQ1,"instanceName":"12"}),makeQuery(id+"F3.opPattern","COPY",FACE,{"derivedFrom":subQ1,"instanceName":"13"}),makeQuery(id+"F3.opPattern","COPY",FACE,{"derivedFrom":subQ1,"instanceName":"14"}),makeQuery(id+"F3.opPattern","COPY",FACE,{"derivedFrom":subQ1,"instanceName":"15"}),makeQuery(id+"F3.opPattern","COPY",FACE,{"derivedFrom":subQ1,"instanceName":"16"}),makeQuery(id+"F3.opPattern","COPY",FACE,{"derivedFrom":subQ1,"instanceName":"17"}),makeQuery(id+"F3.opPattern","COPY",FACE,{"derivedFrom":subQ1,"instanceName":"18"}),makeQuery(id+"F3.opPattern","COPY",FACE,{"derivedFrom":subQ1,"instanceName":"19"}),makeQuery(id+"F3.opPattern","COPY",FACE,{"derivedFrom":subQ1,"instanceName":"20"}),makeQuery(id+"F3.opPattern","COPY",FACE,{"derivedFrom":subQ1,"instanceName":"21"}),makeQuery(id+"F3.opPattern","COPY",FACE,{"derivedFrom":subQ1,"instanceName":"22"}),makeQuery(id+"F3.opPattern","COPY",FACE,{"derivedFrom":subQ1,"instanceName":"23"}),makeQuery(id+"F3.opPattern","COPY",FACE,{"derivedFrom":subQ1,"instanceName":"24"}),makeQuery(id+"F3.opPattern","COPY",FACE,{"derivedFrom":subQ1,"instanceName":"25"}),makeQuery(id+"F3.opPattern","COPY",FACE,{"derivedFrom":subQ1,"instanceName":"26"}),makeQuery(id+"F3.opPattern","COPY",FACE,{"derivedFrom":subQ1,"instanceName":"27"}),makeQuery(id+"F3.opPattern","COPY",FACE,{"derivedFrom":subQ1,"instanceName":"28"}),makeQuery(id+"F3.opPattern","COPY",FACE,{"derivedFrom":subQ1,"instanceName":"29"}),makeQuery(id+"F3.opPattern","COPY",FACE,{"derivedFrom":subQ1,"instanceName":"30"}),makeQuery(id+"F3.opPattern","COPY",FACE,{"derivedFrom":subQ1,"instanceName":"31"}),makeQuery(id+"F3.opPattern","COPY",FACE,{"derivedFrom":subQ1,"instanceName":"32"}),makeQuery(id+"F3.opPattern","COPY",FACE,{"derivedFrom":subQ1,"instanceName":"33"}),makeQuery(id+"F3.opPattern","COPY",FACE,{"derivedFrom":subQ1,"instanceName":"34"}),makeQuery(id+"F3.opPattern","COPY",FACE,{"derivedFrom":subQ1,"instanceName":"35"}),makeQuery(id+"F3.opPattern","COPY",FACE,{"derivedFrom":subQ1,"instanceName":"36"}),makeQuery(id+"F3.opPattern","COPY",FACE,{"derivedFrom":subQ1,"instanceName":"37"}),makeQuery(id+"F3.opPattern","COPY",FACE,{"derivedFrom":subQ1,"instanceName":"38"}),makeQuery(id+"F3.opPattern","COPY",FACE,{"derivedFrom":subQ1,"instanceName":"39"}),makeQuery(id+"F3.opPattern","COPY",FACE,{"derivedFrom":subQ1,"instanceName":"40"}),makeQuery(id+"F3.opPattern","COPY",FACE,{"derivedFrom":subQ1,"instanceName":"41"}),makeQuery(id+"F3.opPattern","COPY",FACE,{"derivedFrom":subQ1,"instanceName":"42"}),makeQuery(id+"F3.opPattern","COPY",FACE,{"derivedFrom":subQ1,"instanceName":"43"}),makeQuery(id+"F3.opPattern","COPY",FACE,{"derivedFrom":subQ1,"instanceName":"44"}),makeQuery(id+"F3.opPattern","COPY",FACE,{"derivedFrom":subQ1,"instanceName":"45"}),makeQuery(id+"F3.opPattern","COPY",FACE,{"derivedFrom":subQ1,"instanceName":"46"}),makeQuery(id+"F3.opPattern","COPY",FACE,{"derivedFrom":subQ1,"instanceName":"47"}),makeQuery(id+"F3.opPattern","COPY",FACE,{"derivedFrom":subQ1,"instanceName":"48"}),makeQuery(id+"F3.opPattern","COPY",FACE,{"derivedFrom":subQ1,"instanceName":"49"}),makeQuery(id+"F3.opPattern","COPY",FACE,{"derivedFrom":subQ1,"instanceName":"50"}),makeQuery(id+"F3.opPattern","COPY",FACE,{"derivedFrom":subQ1,"instanceName":"51"}),makeQuery(id+"F3.opPattern","COPY",FACE,{"derivedFrom":subQ1,"instanceName":"52"}),makeQuery(id+"F3.opPattern","COPY",FACE,{"derivedFrom":subQ1,"instanceName":"53"}),makeQuery(id+"F3.opPattern","COPY",FACE,{"derivedFrom":subQ1,"instanceName":"54"}),makeQuery(id+"F3.opPattern","COPY",FACE,{"derivedFrom":subQ1,"instanceName":"55"}),makeQuery(id+"F3.opPattern","COPY",FACE,{"derivedFrom":subQ1,"instanceName":"56"}),makeQuery(id+"F3.opPattern","COPY",FACE,{"derivedFrom":subQ1,"instanceName":"57"}),makeQuery(id+"F3.opPattern","COPY",FACE,{"derivedFrom":subQ1,"instanceName":"58"}),makeQuery(id+"F3.opPattern","COPY",FACE,{"derivedFrom":subQ1,"instanceName":"59"}),makeQuery(id+"F3.opPattern","COPY",FACE,{"derivedFrom":subQ1,"instanceName":"60"}),makeQuery(id+"F3.opPattern","COPY",FACE,{"derivedFrom":subQ1,"instanceName":"61"}),makeQuery(id+"F3.opPattern","COPY",FACE,{"derivedFrom":subQ1,"instanceName":"62"}),makeQuery(id+"F3.opPattern","COPY",FACE,{"derivedFrom":subQ1,"instanceName":"63"}),makeQuery(id+"F3.opPattern","COPY",FACE,{"derivedFrom":subQ1,"instanceName":"64"}),makeQuery(id+"F3.opPattern","COPY",FACE,{"derivedFrom":subQ1,"instanceName":"65"}),makeQuery(id+"F3.opPattern","COPY",FACE,{"derivedFrom":subQ1,"instanceName":"66"}),makeQuery(id+"F3.opPattern","COPY",FACE,{"derivedFrom":subQ1,"instanceName":"67"}),makeQuery(id+"F3.opPattern","COPY",FACE,{"derivedFrom":subQ1,"instanceName":"68"}),makeQuery(id+"F3.opPattern","COPY",FACE,{"derivedFrom":subQ1,"instanceName":"69"}),makeQuery(id+"F3.opPattern","COPY",FACE,{"derivedFrom":subQ1,"instanceName":"70"}),makeQuery(id+"F3.opPattern","COPY",FACE,{"derivedFrom":subQ1,"instanceName":"71"}),makeQuery(id+"F3.opPattern","COPY",FACE,{"derivedFrom":subQ1,"instanceName":"72"}),makeQuery(id+"F3.opPattern","COPY",FACE,{"derivedFrom":subQ1,"instanceName":"73"}),makeQuery(id+"F3.opPattern","COPY",FACE,{"derivedFrom":subQ1,"instanceName":"74"}),makeQuery(id+"F3.opPattern","COPY",FACE,{"derivedFrom":subQ1,"instanceName":"75"}),makeQuery(id+"F3.opPattern","COPY",FACE,{"derivedFrom":subQ1,"instanceName":"76"}),makeQuery(id+"F3.opPattern","COPY",FACE,{"derivedFrom":subQ1,"instanceName":"77"}),makeQuery(id+"F3.opPattern","COPY",FACE,{"derivedFrom":subQ1,"instanceName":"78"}),makeQuery(id+"F3.opPattern","COPY",FACE,{"derivedFrom":subQ1,"instanceName":"79"}),makeQuery(id+"F3.opPattern","COPY",FACE,{"derivedFrom":subQ1,"instanceName":"80"}),makeQuery(id+"F3.opPattern","COPY",FACE,{"derivedFrom":subQ1,"instanceName":"81"}),makeQuery(id+"F3.opPattern","COPY",FACE,{"derivedFrom":subQ1,"instanceName":"82"}),makeQuery(id+"F3.opPattern","COPY",FACE,{"derivedFrom":subQ1,"instanceName":"83"}),makeQuery(id+"F3.opPattern","COPY",FACE,{"derivedFrom":subQ1,"instanceName":"84"}),makeQuery(id+"F3.opPattern","COPY",FACE,{"derivedFrom":subQ1,"instanceName":"85"}),makeQuery(id+"F3.opPattern","COPY",FACE,{"derivedFrom":subQ1,"instanceName":"86"}),makeQuery(id+"F3.opPattern","COPY",FACE,{"derivedFrom":subQ1,"instanceName":"87"}),makeQuery(id+"F3.opPattern","COPY",FACE,{"derivedFrom":subQ1,"instanceName":"88"}),makeQuery(id+"F3.opPattern","COPY",FACE,{"derivedFrom":subQ1,"instanceName":"89"}),makeQuery(id+"F3.opPattern","COPY",FACE,{"derivedFrom":subQ1,"instanceName":"90"}),makeQuery(id+"F3.opPattern","COPY",FACE,{"derivedFrom":subQ1,"instanceName":"91"}),makeQuery(id+"F3.opPattern","COPY",FACE,{"derivedFrom":subQ1,"instanceName":"92"}),makeQuery(id+"F3.opPattern","COPY",FACE,{"derivedFrom":subQ1,"instanceName":"93"}),makeQuery(id+"F3.opPattern","COPY",FACE,{"derivedFrom":subQ1,"instanceName":"94"}),makeQuery(id+"F3.opPattern","COPY",FACE,{"derivedFrom":subQ1,"instanceName":"95"}),makeQuery(id+"F3.opPattern","COPY",FACE,{"derivedFrom":subQ1,"instanceName":"96"}),makeQuery(id+"F3.opPattern","COPY",FACE,{"derivedFrom":subQ1,"instanceName":"97"}),makeQuery(id+"F3.opPattern","COPY",FACE,{"derivedFrom":subQ1,"instanceName":"98"}),makeQuery(id+"F3.opPattern","COPY",FACE,{"derivedFrom":subQ1,"instanceName":"99"}),makeQuery(id+"F3.opPattern","COPY",FACE,{"derivedFrom":subQ1,"instanceName":"100"}),makeQuery(id+"F3.opPattern","COPY",FACE,{"derivedFrom":subQ1,"instanceName":"101"}),makeQuery(id+"F3.opPattern","COPY",FACE,{"derivedFrom":subQ1,"instanceName":"102"}),makeQuery(id+"F3.opPattern","COPY",FACE,{"derivedFrom":subQ1,"instanceName":"103"}),makeQuery(id+"F3.opPattern","COPY",FACE,{"derivedFrom":subQ1,"instanceName":"104"}),makeQuery(id+"F3.opPattern","COPY",FACE,{"derivedFrom":subQ1,"instanceName":"105"}),makeQuery(id+"F3.opPattern","COPY",FACE,{"derivedFrom":subQ1,"instanceName":"106"}),makeQuery(id+"F3.opPattern","COPY",FACE,{"derivedFrom":subQ1,"instanceName":"107"}),makeQuery(id+"F3.opPattern","COPY",FACE,{"derivedFrom":subQ1,"instanceName":"108"}),makeQuery(id+"F3.opPattern","COPY",FACE,{"derivedFrom":subQ1,"instanceName":"109"}),makeQuery(id+"F3.opPattern","COPY",FACE,{"derivedFrom":subQ1,"instanceName":"110"}),makeQuery(id+"F3.opPattern","COPY",FACE,{"derivedFrom":subQ1,"instanceName":"111"}),makeQuery(id+"F3.opPattern","COPY",FACE,{"derivedFrom":subQ1,"instanceName":"112"}),makeQuery(id+"F3.opPattern","COPY",FACE,{"derivedFrom":subQ1,"instanceName":"113"}),makeQuery(id+"F3.opPattern","COPY",FACE,{"derivedFrom":subQ1,"instanceName":"114"}),makeQuery(id+"F3.opPattern","COPY",FACE,{"derivedFrom":subQ1,"instanceName":"115"}),makeQuery(id+"F3.opPattern","COPY",FACE,{"derivedFrom":subQ1,"instanceName":"116"}),makeQuery(id+"F3.opPattern","COPY",FACE,{"derivedFrom":subQ1,"instanceName":"117"}),makeQuery(id+"F3.opPattern","COPY",FACE,{"derivedFrom":subQ1,"instanceName":"118"}),makeQuery(id+"F3.opPattern","COPY",FACE,{"derivedFrom":subQ1,"instanceName":"119"}),makeQuery(id+"F3.opPattern","COPY",FACE,{"derivedFrom":subQ1,"instanceName":"120"}),makeQuery(id+"F3.opPattern","COPY",FACE,{"derivedFrom":subQ1,"instanceName":"121"}),makeQuery(id+"F3.opPattern","COPY",FACE,{"derivedFrom":subQ1,"instanceName":"122"}),makeQuery(id+"F3.opPattern","COPY",FACE,{"derivedFrom":subQ1,"instanceName":"123"}),makeQuery(id+"F3.opPattern","COPY",FACE,{"derivedFrom":subQ1,"instanceName":"124"}),makeQuery(id+"F3.opPattern","COPY",FACE,{"derivedFrom":subQ1,"instanceName":"125"}),makeQuery(id+"F3.opPattern","COPY",FACE,{"derivedFrom":subQ1,"instanceName":"126"}),makeQuery(id+"F3.opPattern","COPY",FACE,{"derivedFrom":subQ1,"instanceName":"127"}),makeQuery(id+"F3.opPattern","COPY",FACE,{"derivedFrom":subQ1,"instanceName":"128"}),makeQuery(id+"F3.opPattern","COPY",FACE,{"derivedFrom":subQ1,"instanceName":"129"}),makeQuery(id+"F3.opPattern","COPY",FACE,{"derivedFrom":subQ1,"instanceName":"130"}),makeQuery(id+"F3.opPattern","COPY",FACE,{"derivedFrom":subQ1,"instanceName":"131"})]});}
            var sketch = newSketch(context, id + "F10", { "sketchPlane" : qUnion([Q0])});
            skArc(sketch, "E27", {"start": v(-10.66, 28.02) * mm, "mid": v(-14.99, 25.96) * mm, "end": v(-18.93, 23.24) * mm});
            skArc(sketch, "E28.0", {"start": v(18.93, 23.24) * mm, "mid": v(19.25, 11.11) * mm, "end": v(29.6, 4.78) * mm});
            skArc(sketch, "E29.0", {"start": v(-10.66, 28.02) * mm, "mid": v(0, 22.23) * mm, "end": v(10.66, 28.02) * mm});
            skArc(sketch, "E29.1", {"start": v(-29.78, 4.77) * mm, "mid": v(-19.25, 11.11) * mm, "end": v(-19.02, 23.4) * mm});
            skArc(sketch, "E29.2", {"start": v(-18.93, -23.24) * mm, "mid": v(-19.25, -11.11) * mm, "end": v(-29.6, -4.78) * mm});
            skArc(sketch, "E29.3", {"start": v(10.66, -28.02) * mm, "mid": v(0, -22.23) * mm, "end": v(-10.66, -28.02) * mm});
            skArc(sketch, "E29.4", {"start": v(29.6, -4.78) * mm, "mid": v(19.25, -11.11) * mm, "end": v(18.93, -23.24) * mm});
            skArc(sketch, "E30.trimOffspring", {"start": v(18.93, 23.24) * mm, "mid": v(14.99, 25.96) * mm, "end": v(10.66, 28.02) * mm});
            skArc(sketch, "E31.trimOffspring", {"start": v(29.6, -4.78) * mm, "mid": v(29.97, 0) * mm, "end": v(29.6, 4.78) * mm});
            skArc(sketch, "E32.trimOffspring", {"start": v(10.66, -28.02) * mm, "mid": v(14.99, -25.96) * mm, "end": v(18.93, -23.24) * mm});
            skArc(sketch, "E33.trimOffspring", {"start": v(-18.93, -23.24) * mm, "mid": v(-14.99, -25.96) * mm, "end": v(-10.66, -28.02) * mm});
            skArc(sketch, "E34.trimOffspring", {"start": v(-29.6, 4.78) * mm, "mid": v(-29.97, 0) * mm, "end": v(-29.6, -4.78) * mm});
            skCircle(sketch, "E35.0", {"center": v(-11.9, 20.62) * mm, "radius": 2.41 * mm});
            skCircle(sketch, "E35.1", {"center": v(11.9, 20.62) * mm, "radius": 2.41 * mm});
            skCircle(sketch, "E35.2", {"center": v(23.81, 0) * mm, "radius": 2.41 * mm});
            skCircle(sketch, "E35.3", {"center": v(11.9, -20.62) * mm, "radius": 2.41 * mm});
            skCircle(sketch, "E35.4", {"center": v(-11.9, -20.62) * mm, "radius": 2.41 * mm});
            skCircle(sketch, "E35.5", {"center": v(-23.81, 0) * mm, "radius": 2.41 * mm});
            skCircle(sketch, "E36.0", {"center": v(0, 0) * mm, "radius": 14.29 * mm});
            skSolve(sketch);
        }
        {
            var Q0;
            Q0=qSketchRegion(id+"F10",true);
            extrude(context, id + "F11", {"entities" : qUnion([Q0]), "depth" : 3.17 * mm});
        }
        {
            var Q0;
            Q0=makeQuery(id+"F11.opExtrude","SWEPT_EDGE",EDGE,{"disambiguationData":[OSD([sQuery(id+"F6.wireOp",EDGE,"E16"),sQuery(id+"F6.wireOp",EDGE,"E17"),sQuery(id+"F6.wireOp",EDGE,"E21.0"),sQuery(id+"F6.wireOp",EDGE,"E22.0"),sQuery(id+"F6.wireOp",EDGE,"E24"),sQuery(id+"F10.wireOp",EDGE,"E28.0"),sQuery(id+"F10.wireOp",EDGE,"E30.trimOffspring")])]});
            var Q1;
            Q1=makeQuery(id+"F11.opExtrude","SWEPT_EDGE",EDGE,{"disambiguationData":[OSD([sQuery(id+"F6.wireOp",EDGE,"E16"),sQuery(id+"F6.wireOp",EDGE,"E17"),sQuery(id+"F6.wireOp",EDGE,"E21.0"),sQuery(id+"F6.wireOp",EDGE,"E22.0"),sQuery(id+"F6.wireOp",EDGE,"E24"),sQuery(id+"F10.wireOp",EDGE,"E28.0"),sQuery(id+"F10.wireOp",EDGE,"E31.trimOffspring")])]});
            var Q2;
            Q2=makeQuery(id+"F11.opExtrude","SWEPT_EDGE",EDGE,{"disambiguationData":[OSD([sQuery(id+"F6.wireOp",EDGE,"E16"),sQuery(id+"F6.wireOp",EDGE,"E17"),sQuery(id+"F6.wireOp",EDGE,"E21.0"),sQuery(id+"F6.wireOp",EDGE,"E22.0"),sQuery(id+"F6.wireOp",EDGE,"E24"),sQuery(id+"F10.wireOp",EDGE,"E29.4"),sQuery(id+"F10.wireOp",EDGE,"E31.trimOffspring")])]});
            var Q3;
            Q3=makeQuery(id+"F11.opExtrude","SWEPT_EDGE",EDGE,{"disambiguationData":[OSD([sQuery(id+"F6.wireOp",EDGE,"E16"),sQuery(id+"F6.wireOp",EDGE,"E17"),sQuery(id+"F6.wireOp",EDGE,"E21.0"),sQuery(id+"F6.wireOp",EDGE,"E22.0"),sQuery(id+"F6.wireOp",EDGE,"E24"),sQuery(id+"F10.wireOp",EDGE,"E29.4"),sQuery(id+"F10.wireOp",EDGE,"E32.trimOffspring")])]});
            var Q4;
            Q4=makeQuery(id+"F11.opExtrude","SWEPT_EDGE",EDGE,{"disambiguationData":[OSD([sQuery(id+"F6.wireOp",EDGE,"E16"),sQuery(id+"F6.wireOp",EDGE,"E17"),sQuery(id+"F6.wireOp",EDGE,"E21.0"),sQuery(id+"F6.wireOp",EDGE,"E22.0"),sQuery(id+"F6.wireOp",EDGE,"E24"),sQuery(id+"F10.wireOp",EDGE,"E29.3"),sQuery(id+"F10.wireOp",EDGE,"E32.trimOffspring")])]});
            var Q5;
            Q5=makeQuery(id+"F11.opExtrude","SWEPT_EDGE",EDGE,{"disambiguationData":[OSD([sQuery(id+"F6.wireOp",EDGE,"E16"),sQuery(id+"F6.wireOp",EDGE,"E17"),sQuery(id+"F6.wireOp",EDGE,"E21.0"),sQuery(id+"F6.wireOp",EDGE,"E22.0"),sQuery(id+"F6.wireOp",EDGE,"E24"),sQuery(id+"F10.wireOp",EDGE,"E29.3"),sQuery(id+"F10.wireOp",EDGE,"E33.trimOffspring")])]});
            var Q6;
            Q6=makeQuery(id+"F11.opExtrude","SWEPT_EDGE",EDGE,{"disambiguationData":[OSD([sQuery(id+"F6.wireOp",EDGE,"E16"),sQuery(id+"F6.wireOp",EDGE,"E17"),sQuery(id+"F6.wireOp",EDGE,"E21.0"),sQuery(id+"F6.wireOp",EDGE,"E22.0"),sQuery(id+"F6.wireOp",EDGE,"E24"),sQuery(id+"F10.wireOp",EDGE,"E29.2"),sQuery(id+"F10.wireOp",EDGE,"E33.trimOffspring")])]});
            var Q7;
            Q7=makeQuery(id+"F11.opExtrude","SWEPT_EDGE",EDGE,{"disambiguationData":[OSD([sQuery(id+"F6.wireOp",EDGE,"E16"),sQuery(id+"F6.wireOp",EDGE,"E17"),sQuery(id+"F6.wireOp",EDGE,"E21.0"),sQuery(id+"F6.wireOp",EDGE,"E22.0"),sQuery(id+"F6.wireOp",EDGE,"E24"),sQuery(id+"F10.wireOp",EDGE,"E29.2"),sQuery(id+"F10.wireOp",EDGE,"E34.trimOffspring")])]});
            var Q8;
            Q8=makeQuery(id+"F11.opExtrude","SWEPT_EDGE",EDGE,{"disambiguationData":[OSD([sQuery(id+"F6.wireOp",EDGE,"E16"),sQuery(id+"F6.wireOp",EDGE,"E17"),sQuery(id+"F6.wireOp",EDGE,"E21.0"),sQuery(id+"F6.wireOp",EDGE,"E22.0"),sQuery(id+"F6.wireOp",EDGE,"E24"),sQuery(id+"F10.wireOp",EDGE,"E29.1"),sQuery(id+"F10.wireOp",EDGE,"E34.trimOffspring")])]});
            var Q9;
            Q9=makeQuery(id+"F11.opExtrude","SWEPT_EDGE",EDGE,{"disambiguationData":[OSD([sQuery(id+"F6.wireOp",EDGE,"E16"),sQuery(id+"F6.wireOp",EDGE,"E17"),sQuery(id+"F6.wireOp",EDGE,"E21.0"),sQuery(id+"F6.wireOp",EDGE,"E22.0"),sQuery(id+"F6.wireOp",EDGE,"E24"),sQuery(id+"F10.wireOp",EDGE,"E27"),sQuery(id+"F10.wireOp",EDGE,"E29.1")])]});
            var Q10;
            Q10=makeQuery(id+"F11.opExtrude","SWEPT_EDGE",EDGE,{"disambiguationData":[OSD([sQuery(id+"F6.wireOp",EDGE,"E16"),sQuery(id+"F6.wireOp",EDGE,"E17"),sQuery(id+"F6.wireOp",EDGE,"E21.0"),sQuery(id+"F6.wireOp",EDGE,"E22.0"),sQuery(id+"F6.wireOp",EDGE,"E24"),sQuery(id+"F10.wireOp",EDGE,"E27"),sQuery(id+"F10.wireOp",EDGE,"E29.0")])]});
            var Q11;
            Q11=makeQuery(id+"F11.opExtrude","SWEPT_EDGE",EDGE,{"disambiguationData":[OSD([sQuery(id+"F6.wireOp",EDGE,"E16"),sQuery(id+"F6.wireOp",EDGE,"E17"),sQuery(id+"F6.wireOp",EDGE,"E21.0"),sQuery(id+"F6.wireOp",EDGE,"E22.0"),sQuery(id+"F6.wireOp",EDGE,"E24"),sQuery(id+"F10.wireOp",EDGE,"E29.0"),sQuery(id+"F10.wireOp",EDGE,"E30.trimOffspring")])]});
            fillet(context, id + "F12", {"entities" : qUnion([Q0, Q1, Q2, Q3, Q4, Q5, Q6, Q7, Q8, Q9, Q10, Q11]), "radius" : 1.59 * mm, "tangentPropagation" : true, "allowEdgeOverflow" : false});
        }
        {
            var Q0;
            {var subQ0=sQuery(id+"F0.wireOp",EDGE,"E7");var subQ1=makeQuery(id+"F2.opExtrude","CAP_FACE",FACE,{"disambiguationData":[OSD([sQuery(id+"F0.wireOp",EDGE,"E2"),sQuery(id+"F0.wireOp",EDGE,"E3"),sQuery(id+"F0.wireOp",EDGE,"E4"),sQuery(id+"F0.wireOp",EDGE,"E5"),sQuery(id+"F0.wireOp",EDGE,"E6"),subQ0])],"isStart":true});Q0=makeQuery(id+"F3.boolean.opBoolean","MERGE",FACE,{"derivedFrom":[makeQuery(id+"F1.opExtrude","CAP_FACE",FACE,{"disambiguationData":[OSD([sQuery(id+"F0.wireOp",EDGE,"E0"),sQuery(id+"F0.wireOp",EDGE,"E1"),subQ0])],"isStart":true}),subQ1,makeQuery(id+"F3.opPattern","COPY",FACE,{"derivedFrom":subQ1,"instanceName":"1"}),makeQuery(id+"F3.opPattern","COPY",FACE,{"derivedFrom":subQ1,"instanceName":"2"}),makeQuery(id+"F3.opPattern","COPY",FACE,{"derivedFrom":subQ1,"instanceName":"3"}),makeQuery(id+"F3.opPattern","COPY",FACE,{"derivedFrom":subQ1,"instanceName":"4"}),makeQuery(id+"F3.opPattern","COPY",FACE,{"derivedFrom":subQ1,"instanceName":"5"}),makeQuery(id+"F3.opPattern","COPY",FACE,{"derivedFrom":subQ1,"instanceName":"6"}),makeQuery(id+"F3.opPattern","COPY",FACE,{"derivedFrom":subQ1,"instanceName":"7"}),makeQuery(id+"F3.opPattern","COPY",FACE,{"derivedFrom":subQ1,"instanceName":"8"}),makeQuery(id+"F3.opPattern","COPY",FACE,{"derivedFrom":subQ1,"instanceName":"9"}),makeQuery(id+"F3.opPattern","COPY",FACE,{"derivedFrom":subQ1,"instanceName":"10"}),makeQuery(id+"F3.opPattern","COPY",FACE,{"derivedFrom":subQ1,"instanceName":"11"}),makeQuery(id+"F3.opPattern","COPY",FACE,{"derivedFrom":subQ1,"instanceName":"12"}),makeQuery(id+"F3.opPattern","COPY",FACE,{"derivedFrom":subQ1,"instanceName":"13"}),makeQuery(id+"F3.opPattern","COPY",FACE,{"derivedFrom":subQ1,"instanceName":"14"}),makeQuery(id+"F3.opPattern","COPY",FACE,{"derivedFrom":subQ1,"instanceName":"15"}),makeQuery(id+"F3.opPattern","COPY",FACE,{"derivedFrom":subQ1,"instanceName":"16"}),makeQuery(id+"F3.opPattern","COPY",FACE,{"derivedFrom":subQ1,"instanceName":"17"}),makeQuery(id+"F3.opPattern","COPY",FACE,{"derivedFrom":subQ1,"instanceName":"18"}),makeQuery(id+"F3.opPattern","COPY",FACE,{"derivedFrom":subQ1,"instanceName":"19"}),makeQuery(id+"F3.opPattern","COPY",FACE,{"derivedFrom":subQ1,"instanceName":"20"}),makeQuery(id+"F3.opPattern","COPY",FACE,{"derivedFrom":subQ1,"instanceName":"21"}),makeQuery(id+"F3.opPattern","COPY",FACE,{"derivedFrom":subQ1,"instanceName":"22"}),makeQuery(id+"F3.opPattern","COPY",FACE,{"derivedFrom":subQ1,"instanceName":"23"}),makeQuery(id+"F3.opPattern","COPY",FACE,{"derivedFrom":subQ1,"instanceName":"24"}),makeQuery(id+"F3.opPattern","COPY",FACE,{"derivedFrom":subQ1,"instanceName":"25"}),makeQuery(id+"F3.opPattern","COPY",FACE,{"derivedFrom":subQ1,"instanceName":"26"}),makeQuery(id+"F3.opPattern","COPY",FACE,{"derivedFrom":subQ1,"instanceName":"27"}),makeQuery(id+"F3.opPattern","COPY",FACE,{"derivedFrom":subQ1,"instanceName":"28"}),makeQuery(id+"F3.opPattern","COPY",FACE,{"derivedFrom":subQ1,"instanceName":"29"}),makeQuery(id+"F3.opPattern","COPY",FACE,{"derivedFrom":subQ1,"instanceName":"30"}),makeQuery(id+"F3.opPattern","COPY",FACE,{"derivedFrom":subQ1,"instanceName":"31"}),makeQuery(id+"F3.opPattern","COPY",FACE,{"derivedFrom":subQ1,"instanceName":"32"}),makeQuery(id+"F3.opPattern","COPY",FACE,{"derivedFrom":subQ1,"instanceName":"33"}),makeQuery(id+"F3.opPattern","COPY",FACE,{"derivedFrom":subQ1,"instanceName":"34"}),makeQuery(id+"F3.opPattern","COPY",FACE,{"derivedFrom":subQ1,"instanceName":"35"}),makeQuery(id+"F3.opPattern","COPY",FACE,{"derivedFrom":subQ1,"instanceName":"36"}),makeQuery(id+"F3.opPattern","COPY",FACE,{"derivedFrom":subQ1,"instanceName":"37"}),makeQuery(id+"F3.opPattern","COPY",FACE,{"derivedFrom":subQ1,"instanceName":"38"}),makeQuery(id+"F3.opPattern","COPY",FACE,{"derivedFrom":subQ1,"instanceName":"39"}),makeQuery(id+"F3.opPattern","COPY",FACE,{"derivedFrom":subQ1,"instanceName":"40"}),makeQuery(id+"F3.opPattern","COPY",FACE,{"derivedFrom":subQ1,"instanceName":"41"}),makeQuery(id+"F3.opPattern","COPY",FACE,{"derivedFrom":subQ1,"instanceName":"42"}),makeQuery(id+"F3.opPattern","COPY",FACE,{"derivedFrom":subQ1,"instanceName":"43"}),makeQuery(id+"F3.opPattern","COPY",FACE,{"derivedFrom":subQ1,"instanceName":"44"}),makeQuery(id+"F3.opPattern","COPY",FACE,{"derivedFrom":subQ1,"instanceName":"45"}),makeQuery(id+"F3.opPattern","COPY",FACE,{"derivedFrom":subQ1,"instanceName":"46"}),makeQuery(id+"F3.opPattern","COPY",FACE,{"derivedFrom":subQ1,"instanceName":"47"}),makeQuery(id+"F3.opPattern","COPY",FACE,{"derivedFrom":subQ1,"instanceName":"48"}),makeQuery(id+"F3.opPattern","COPY",FACE,{"derivedFrom":subQ1,"instanceName":"49"}),makeQuery(id+"F3.opPattern","COPY",FACE,{"derivedFrom":subQ1,"instanceName":"50"}),makeQuery(id+"F3.opPattern","COPY",FACE,{"derivedFrom":subQ1,"instanceName":"51"}),makeQuery(id+"F3.opPattern","COPY",FACE,{"derivedFrom":subQ1,"instanceName":"52"}),makeQuery(id+"F3.opPattern","COPY",FACE,{"derivedFrom":subQ1,"instanceName":"53"}),makeQuery(id+"F3.opPattern","COPY",FACE,{"derivedFrom":subQ1,"instanceName":"54"}),makeQuery(id+"F3.opPattern","COPY",FACE,{"derivedFrom":subQ1,"instanceName":"55"}),makeQuery(id+"F3.opPattern","COPY",FACE,{"derivedFrom":subQ1,"instanceName":"56"}),makeQuery(id+"F3.opPattern","COPY",FACE,{"derivedFrom":subQ1,"instanceName":"57"}),makeQuery(id+"F3.opPattern","COPY",FACE,{"derivedFrom":subQ1,"instanceName":"58"}),makeQuery(id+"F3.opPattern","COPY",FACE,{"derivedFrom":subQ1,"instanceName":"59"}),makeQuery(id+"F3.opPattern","COPY",FACE,{"derivedFrom":subQ1,"instanceName":"60"}),makeQuery(id+"F3.opPattern","COPY",FACE,{"derivedFrom":subQ1,"instanceName":"61"}),makeQuery(id+"F3.opPattern","COPY",FACE,{"derivedFrom":subQ1,"instanceName":"62"}),makeQuery(id+"F3.opPattern","COPY",FACE,{"derivedFrom":subQ1,"instanceName":"63"}),makeQuery(id+"F3.opPattern","COPY",FACE,{"derivedFrom":subQ1,"instanceName":"64"}),makeQuery(id+"F3.opPattern","COPY",FACE,{"derivedFrom":subQ1,"instanceName":"65"}),makeQuery(id+"F3.opPattern","COPY",FACE,{"derivedFrom":subQ1,"instanceName":"66"}),makeQuery(id+"F3.opPattern","COPY",FACE,{"derivedFrom":subQ1,"instanceName":"67"}),makeQuery(id+"F3.opPattern","COPY",FACE,{"derivedFrom":subQ1,"instanceName":"68"}),makeQuery(id+"F3.opPattern","COPY",FACE,{"derivedFrom":subQ1,"instanceName":"69"}),makeQuery(id+"F3.opPattern","COPY",FACE,{"derivedFrom":subQ1,"instanceName":"70"}),makeQuery(id+"F3.opPattern","COPY",FACE,{"derivedFrom":subQ1,"instanceName":"71"}),makeQuery(id+"F3.opPattern","COPY",FACE,{"derivedFrom":subQ1,"instanceName":"72"}),makeQuery(id+"F3.opPattern","COPY",FACE,{"derivedFrom":subQ1,"instanceName":"73"}),makeQuery(id+"F3.opPattern","COPY",FACE,{"derivedFrom":subQ1,"instanceName":"74"}),makeQuery(id+"F3.opPattern","COPY",FACE,{"derivedFrom":subQ1,"instanceName":"75"}),makeQuery(id+"F3.opPattern","COPY",FACE,{"derivedFrom":subQ1,"instanceName":"76"}),makeQuery(id+"F3.opPattern","COPY",FACE,{"derivedFrom":subQ1,"instanceName":"77"}),makeQuery(id+"F3.opPattern","COPY",FACE,{"derivedFrom":subQ1,"instanceName":"78"}),makeQuery(id+"F3.opPattern","COPY",FACE,{"derivedFrom":subQ1,"instanceName":"79"}),makeQuery(id+"F3.opPattern","COPY",FACE,{"derivedFrom":subQ1,"instanceName":"80"}),makeQuery(id+"F3.opPattern","COPY",FACE,{"derivedFrom":subQ1,"instanceName":"81"}),makeQuery(id+"F3.opPattern","COPY",FACE,{"derivedFrom":subQ1,"instanceName":"82"}),makeQuery(id+"F3.opPattern","COPY",FACE,{"derivedFrom":subQ1,"instanceName":"83"}),makeQuery(id+"F3.opPattern","COPY",FACE,{"derivedFrom":subQ1,"instanceName":"84"}),makeQuery(id+"F3.opPattern","COPY",FACE,{"derivedFrom":subQ1,"instanceName":"85"}),makeQuery(id+"F3.opPattern","COPY",FACE,{"derivedFrom":subQ1,"instanceName":"86"}),makeQuery(id+"F3.opPattern","COPY",FACE,{"derivedFrom":subQ1,"instanceName":"87"}),makeQuery(id+"F3.opPattern","COPY",FACE,{"derivedFrom":subQ1,"instanceName":"88"}),makeQuery(id+"F3.opPattern","COPY",FACE,{"derivedFrom":subQ1,"instanceName":"89"}),makeQuery(id+"F3.opPattern","COPY",FACE,{"derivedFrom":subQ1,"instanceName":"90"}),makeQuery(id+"F3.opPattern","COPY",FACE,{"derivedFrom":subQ1,"instanceName":"91"}),makeQuery(id+"F3.opPattern","COPY",FACE,{"derivedFrom":subQ1,"instanceName":"92"}),makeQuery(id+"F3.opPattern","COPY",FACE,{"derivedFrom":subQ1,"instanceName":"93"}),makeQuery(id+"F3.opPattern","COPY",FACE,{"derivedFrom":subQ1,"instanceName":"94"}),makeQuery(id+"F3.opPattern","COPY",FACE,{"derivedFrom":subQ1,"instanceName":"95"}),makeQuery(id+"F3.opPattern","COPY",FACE,{"derivedFrom":subQ1,"instanceName":"96"}),makeQuery(id+"F3.opPattern","COPY",FACE,{"derivedFrom":subQ1,"instanceName":"97"}),makeQuery(id+"F3.opPattern","COPY",FACE,{"derivedFrom":subQ1,"instanceName":"98"}),makeQuery(id+"F3.opPattern","COPY",FACE,{"derivedFrom":subQ1,"instanceName":"99"}),makeQuery(id+"F3.opPattern","COPY",FACE,{"derivedFrom":subQ1,"instanceName":"100"}),makeQuery(id+"F3.opPattern","COPY",FACE,{"derivedFrom":subQ1,"instanceName":"101"}),makeQuery(id+"F3.opPattern","COPY",FACE,{"derivedFrom":subQ1,"instanceName":"102"}),makeQuery(id+"F3.opPattern","COPY",FACE,{"derivedFrom":subQ1,"instanceName":"103"}),makeQuery(id+"F3.opPattern","COPY",FACE,{"derivedFrom":subQ1,"instanceName":"104"}),makeQuery(id+"F3.opPattern","COPY",FACE,{"derivedFrom":subQ1,"instanceName":"105"}),makeQuery(id+"F3.opPattern","COPY",FACE,{"derivedFrom":subQ1,"instanceName":"106"}),makeQuery(id+"F3.opPattern","COPY",FACE,{"derivedFrom":subQ1,"instanceName":"107"}),makeQuery(id+"F3.opPattern","COPY",FACE,{"derivedFrom":subQ1,"instanceName":"108"}),makeQuery(id+"F3.opPattern","COPY",FACE,{"derivedFrom":subQ1,"instanceName":"109"}),makeQuery(id+"F3.opPattern","COPY",FACE,{"derivedFrom":subQ1,"instanceName":"110"}),makeQuery(id+"F3.opPattern","COPY",FACE,{"derivedFrom":subQ1,"instanceName":"111"}),makeQuery(id+"F3.opPattern","COPY",FACE,{"derivedFrom":subQ1,"instanceName":"112"}),makeQuery(id+"F3.opPattern","COPY",FACE,{"derivedFrom":subQ1,"instanceName":"113"}),makeQuery(id+"F3.opPattern","COPY",FACE,{"derivedFrom":subQ1,"instanceName":"114"}),makeQuery(id+"F3.opPattern","COPY",FACE,{"derivedFrom":subQ1,"instanceName":"115"}),makeQuery(id+"F3.opPattern","COPY",FACE,{"derivedFrom":subQ1,"instanceName":"116"}),makeQuery(id+"F3.opPattern","COPY",FACE,{"derivedFrom":subQ1,"instanceName":"117"}),makeQuery(id+"F3.opPattern","COPY",FACE,{"derivedFrom":subQ1,"instanceName":"118"}),makeQuery(id+"F3.opPattern","COPY",FACE,{"derivedFrom":subQ1,"instanceName":"119"}),makeQuery(id+"F3.opPattern","COPY",FACE,{"derivedFrom":subQ1,"instanceName":"120"}),makeQuery(id+"F3.opPattern","COPY",FACE,{"derivedFrom":subQ1,"instanceName":"121"}),makeQuery(id+"F3.opPattern","COPY",FACE,{"derivedFrom":subQ1,"instanceName":"122"}),makeQuery(id+"F3.opPattern","COPY",FACE,{"derivedFrom":subQ1,"instanceName":"123"}),makeQuery(id+"F3.opPattern","COPY",FACE,{"derivedFrom":subQ1,"instanceName":"124"}),makeQuery(id+"F3.opPattern","COPY",FACE,{"derivedFrom":subQ1,"instanceName":"125"}),makeQuery(id+"F3.opPattern","COPY",FACE,{"derivedFrom":subQ1,"instanceName":"126"}),makeQuery(id+"F3.opPattern","COPY",FACE,{"derivedFrom":subQ1,"instanceName":"127"}),makeQuery(id+"F3.opPattern","COPY",FACE,{"derivedFrom":subQ1,"instanceName":"128"}),makeQuery(id+"F3.opPattern","COPY",FACE,{"derivedFrom":subQ1,"instanceName":"129"}),makeQuery(id+"F3.opPattern","COPY",FACE,{"derivedFrom":subQ1,"instanceName":"130"}),makeQuery(id+"F3.opPattern","COPY",FACE,{"derivedFrom":subQ1,"instanceName":"131"})]});}
            var sketch = newSketch(context, id + "F13", { "sketchPlane" : qUnion([Q0])});
            skCircle(sketch, "E37.0", {"center": v(-23.81, 0) * mm, "radius": 2.41 * mm});
            skCircle(sketch, "E37.1", {"center": v(-11.9, 20.62) * mm, "radius": 2.41 * mm});
            skCircle(sketch, "E37.2", {"center": v(11.9, 20.62) * mm, "radius": 2.41 * mm});
            skCircle(sketch, "E37.3", {"center": v(23.81, 0) * mm, "radius": 2.41 * mm});
            skCircle(sketch, "E37.4", {"center": v(11.9, -20.62) * mm, "radius": 2.41 * mm});
            skCircle(sketch, "E37.5", {"center": v(-11.9, -20.62) * mm, "radius": 2.41 * mm});
            skSolve(sketch);
        }
        {
            var Q0;
            Q0=sQuery(id+"F13.wireOp",VERTEX,"E37.4.center");
            var Q1;
            Q1=sQuery(id+"F13.wireOp",VERTEX,"E37.3.center");
            var Q2;
            Q2=sQuery(id+"F13.wireOp",VERTEX,"E37.2.center");
            var Q3;
            Q3=sQuery(id+"F13.wireOp",VERTEX,"E37.1.center");
            var Q4;
            Q4=sQuery(id+"F13.wireOp",VERTEX,"E37.0.center");
            var Q5;
            Q5=sQuery(id+"F13.wireOp",VERTEX,"E37.5.center");
            var Q6;
            Q6=makeQuery(id+"F1.opExtrude","SWEPT_BODY",BODY,{"disambiguationData":[OSD([sQuery(id+"F0.wireOp",EDGE,"E0"),sQuery(id+"F0.wireOp",EDGE,"E1"),sQuery(id+"F0.wireOp",EDGE,"E7")])]});
            hole(context, id + "F14", {"style" : HoleStyle.C_BORE, "holeDiameter" : 4.83 * mm, "cBoreDiameter" : 7.94 * mm, "cBoreDepth" : 4.83 * mm, "endStyle" : HoleEndStyle.THROUGH, "locations" : qUnion([Q0, Q1, Q2, Q3, Q4, Q5]), "scope" : qUnion([Q6])});
        }
    });
